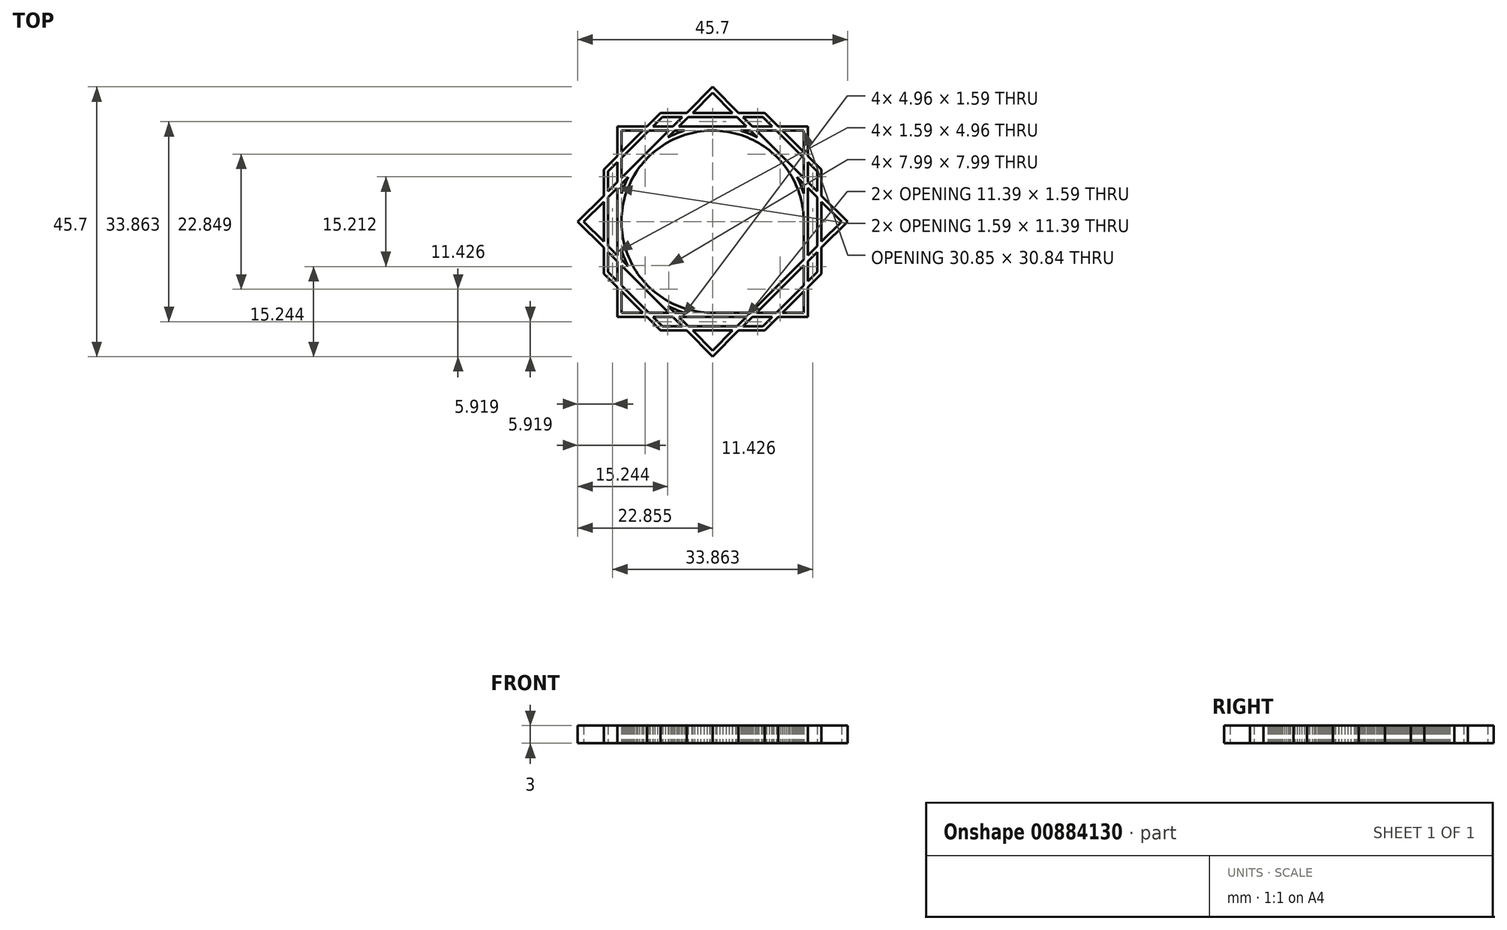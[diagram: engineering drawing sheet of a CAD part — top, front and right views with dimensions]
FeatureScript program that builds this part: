
annotation { "Feature Type Name" : "Feature", "Feature Type Description" : "" }
export const myFeature = defineFeature(function(context is Context, id is Id, definition is map)
    precondition{}
    {
        {
            var Q0;
            Q0=qCreatedBy(makeId("Top.planeOp"),FACE);
            var sketch = newSketch(context, id + "F0", { "sketchPlane" : qUnion([Q0])});
            skLineSegment(sketch, "E0", {"start": v(15.43, 0) * mm, "end": v(15.42, -0.54) * mm});
            skLineSegment(sketch, "E1", {"start": v(15.42, -0.54) * mm, "end": v(15.4, -1.07) * mm});
            skLineSegment(sketch, "E2", {"start": v(15.4, -1.07) * mm, "end": v(15.35, -1.6) * mm});
            skLineSegment(sketch, "E3", {"start": v(15.35, -1.6) * mm, "end": v(15.28, -2.14) * mm});
            skLineSegment(sketch, "E4", {"start": v(15.28, -2.14) * mm, "end": v(15.2, -2.66) * mm});
            skLineSegment(sketch, "E5", {"start": v(15.2, -2.66) * mm, "end": v(15.1, -3.2) * mm});
            skLineSegment(sketch, "E6", {"start": v(15.1, -3.2) * mm, "end": v(14.98, -3.71) * mm});
            skLineSegment(sketch, "E7", {"start": v(14.98, -3.71) * mm, "end": v(14.84, -4.23) * mm});
            skLineSegment(sketch, "E8", {"start": v(14.84, -4.23) * mm, "end": v(14.68, -4.74) * mm});
            skLineSegment(sketch, "E9", {"start": v(14.68, -4.74) * mm, "end": v(14.5, -5.25) * mm});
            skLineSegment(sketch, "E10", {"start": v(14.5, -5.25) * mm, "end": v(14.32, -5.75) * mm});
            skLineSegment(sketch, "E11", {"start": v(14.32, -5.75) * mm, "end": v(14.1, -6.24) * mm});
            skLineSegment(sketch, "E12", {"start": v(14.1, -6.24) * mm, "end": v(13.88, -6.73) * mm});
            skLineSegment(sketch, "E13", {"start": v(13.88, -6.73) * mm, "end": v(13.64, -7.2) * mm});
            skLineSegment(sketch, "E14", {"start": v(13.64, -7.2) * mm, "end": v(13.38, -7.68) * mm});
            skLineSegment(sketch, "E15", {"start": v(13.38, -7.68) * mm, "end": v(13.1, -8.14) * mm});
            skLineSegment(sketch, "E16", {"start": v(13.1, -8.14) * mm, "end": v(12.82, -8.59) * mm});
            skLineSegment(sketch, "E17", {"start": v(12.82, -8.59) * mm, "end": v(12.51, -9.03) * mm});
            skLineSegment(sketch, "E18", {"start": v(12.51, -9.03) * mm, "end": v(12.2, -9.45) * mm});
            skLineSegment(sketch, "E19", {"start": v(12.2, -9.45) * mm, "end": v(11.86, -9.87) * mm});
            skLineSegment(sketch, "E20", {"start": v(11.86, -9.87) * mm, "end": v(11.5, -10.28) * mm});
            skLineSegment(sketch, "E21", {"start": v(11.5, -10.28) * mm, "end": v(11.14, -10.67) * mm});
            skLineSegment(sketch, "E22", {"start": v(11.14, -10.67) * mm, "end": v(10.77, -11.05) * mm});
            skLineSegment(sketch, "E23", {"start": v(10.77, -11.05) * mm, "end": v(10.38, -11.42) * mm});
            skLineSegment(sketch, "E24", {"start": v(10.38, -11.42) * mm, "end": v(9.97, -11.77) * mm});
            skLineSegment(sketch, "E25", {"start": v(9.97, -11.77) * mm, "end": v(9.56, -12.11) * mm});
            skLineSegment(sketch, "E26", {"start": v(9.56, -12.11) * mm, "end": v(9.13, -12.44) * mm});
            skLineSegment(sketch, "E27", {"start": v(9.13, -12.44) * mm, "end": v(8.7, -12.74) * mm});
            skLineSegment(sketch, "E28", {"start": v(8.7, -12.74) * mm, "end": v(8.25, -13.04) * mm});
            skLineSegment(sketch, "E29", {"start": v(8.25, -13.04) * mm, "end": v(7.8, -13.32) * mm});
            skLineSegment(sketch, "E30", {"start": v(7.8, -13.32) * mm, "end": v(7.32, -13.58) * mm});
            skLineSegment(sketch, "E31", {"start": v(7.32, -13.58) * mm, "end": v(6.85, -13.83) * mm});
            skLineSegment(sketch, "E32", {"start": v(6.85, -13.83) * mm, "end": v(6.37, -14.06) * mm});
            skLineSegment(sketch, "E33", {"start": v(6.37, -14.06) * mm, "end": v(5.87, -14.27) * mm});
            skLineSegment(sketch, "E34", {"start": v(5.87, -14.27) * mm, "end": v(5.37, -14.46) * mm});
            skLineSegment(sketch, "E35", {"start": v(5.37, -14.46) * mm, "end": v(4.87, -14.64) * mm});
            skLineSegment(sketch, "E36", {"start": v(4.87, -14.64) * mm, "end": v(4.36, -14.8) * mm});
            skLineSegment(sketch, "E37", {"start": v(4.36, -14.8) * mm, "end": v(3.84, -14.94) * mm});
            skLineSegment(sketch, "E38", {"start": v(3.84, -14.94) * mm, "end": v(3.32, -15.07) * mm});
            skLineSegment(sketch, "E39", {"start": v(3.32, -15.07) * mm, "end": v(2.8, -15.17) * mm});
            skLineSegment(sketch, "E40", {"start": v(2.8, -15.17) * mm, "end": v(2.27, -15.26) * mm});
            skLineSegment(sketch, "E41", {"start": v(2.27, -15.26) * mm, "end": v(1.74, -15.33) * mm});
            skLineSegment(sketch, "E42", {"start": v(1.74, -15.33) * mm, "end": v(1.2, -15.38) * mm});
            skLineSegment(sketch, "E43", {"start": v(1.2, -15.38) * mm, "end": v(0.67, -15.41) * mm});
            skLineSegment(sketch, "E44", {"start": v(0.67, -15.41) * mm, "end": v(0.13, -15.43) * mm});
            skLineSegment(sketch, "E45", {"start": v(0.13, -15.43) * mm, "end": v(-0.4, -15.42) * mm});
            skLineSegment(sketch, "E46", {"start": v(-0.4, -15.42) * mm, "end": v(-0.94, -15.4) * mm});
            skLineSegment(sketch, "E47", {"start": v(-0.94, -15.4) * mm, "end": v(-1.47, -15.36) * mm});
            skLineSegment(sketch, "E48", {"start": v(-1.47, -15.36) * mm, "end": v(-2, -15.3) * mm});
            skLineSegment(sketch, "E49", {"start": v(-2, -15.3) * mm, "end": v(-2.53, -15.22) * mm});
            skLineSegment(sketch, "E50", {"start": v(-2.53, -15.22) * mm, "end": v(-3.06, -15.12) * mm});
            skLineSegment(sketch, "E51", {"start": v(-3.06, -15.12) * mm, "end": v(-3.58, -15) * mm});
            skLineSegment(sketch, "E52", {"start": v(-3.58, -15) * mm, "end": v(-4.1, -14.87) * mm});
            skLineSegment(sketch, "E53", {"start": v(-4.1, -14.87) * mm, "end": v(-4.61, -14.72) * mm});
            skLineSegment(sketch, "E54", {"start": v(-4.61, -14.72) * mm, "end": v(-5.12, -14.55) * mm});
            skLineSegment(sketch, "E55", {"start": v(-5.12, -14.55) * mm, "end": v(-5.63, -14.37) * mm});
            skLineSegment(sketch, "E56", {"start": v(-5.63, -14.37) * mm, "end": v(-6.12, -14.16) * mm});
            skLineSegment(sketch, "E57", {"start": v(-6.12, -14.16) * mm, "end": v(-6.6, -13.94) * mm});
            skLineSegment(sketch, "E58", {"start": v(-6.6, -13.94) * mm, "end": v(-7.09, -13.7) * mm});
            skLineSegment(sketch, "E59", {"start": v(-7.09, -13.7) * mm, "end": v(-7.56, -13.45) * mm});
            skLineSegment(sketch, "E60", {"start": v(-7.56, -13.45) * mm, "end": v(-8.02, -13.18) * mm});
            skLineSegment(sketch, "E61", {"start": v(-8.02, -13.18) * mm, "end": v(-8.47, -12.9) * mm});
            skLineSegment(sketch, "E62", {"start": v(-8.47, -12.9) * mm, "end": v(-8.92, -12.6) * mm});
            skLineSegment(sketch, "E63", {"start": v(-8.92, -12.6) * mm, "end": v(-9.35, -12.27) * mm});
            skLineSegment(sketch, "E64", {"start": v(-9.35, -12.27) * mm, "end": v(-9.77, -11.94) * mm});
            skLineSegment(sketch, "E65", {"start": v(-9.77, -11.94) * mm, "end": v(-10.18, -11.6) * mm});
            skLineSegment(sketch, "E66", {"start": v(-10.18, -11.6) * mm, "end": v(-10.57, -11.24) * mm});
            skLineSegment(sketch, "E67", {"start": v(-10.57, -11.24) * mm, "end": v(-10.96, -10.86) * mm});
            skLineSegment(sketch, "E68", {"start": v(-10.96, -10.86) * mm, "end": v(-11.33, -10.48) * mm});
            skLineSegment(sketch, "E69", {"start": v(-11.33, -10.48) * mm, "end": v(-11.68, -10.08) * mm});
            skLineSegment(sketch, "E70", {"start": v(-11.68, -10.08) * mm, "end": v(-12.03, -9.66) * mm});
            skLineSegment(sketch, "E71", {"start": v(-12.03, -9.66) * mm, "end": v(-12.36, -9.24) * mm});
            skLineSegment(sketch, "E72", {"start": v(-12.36, -9.24) * mm, "end": v(-12.67, -8.8) * mm});
            skLineSegment(sketch, "E73", {"start": v(-12.67, -8.8) * mm, "end": v(-12.97, -8.36) * mm});
            skLineSegment(sketch, "E74", {"start": v(-12.97, -8.36) * mm, "end": v(-13.25, -7.9) * mm});
            skLineSegment(sketch, "E75", {"start": v(-13.25, -7.9) * mm, "end": v(-13.52, -7.44) * mm});
            skLineSegment(sketch, "E76", {"start": v(-13.52, -7.44) * mm, "end": v(-13.77, -6.97) * mm});
            skLineSegment(sketch, "E77", {"start": v(-13.77, -6.97) * mm, "end": v(-14, -6.49) * mm});
            skLineSegment(sketch, "E78", {"start": v(-14, -6.49) * mm, "end": v(-14.22, -6) * mm});
            skLineSegment(sketch, "E79", {"start": v(-14.22, -6) * mm, "end": v(-14.42, -5.5) * mm});
            skLineSegment(sketch, "E80", {"start": v(-14.42, -5.5) * mm, "end": v(-14.6, -5) * mm});
            skLineSegment(sketch, "E81", {"start": v(-14.6, -5) * mm, "end": v(-14.76, -4.49) * mm});
            skLineSegment(sketch, "E82", {"start": v(-14.76, -4.49) * mm, "end": v(-14.9, -3.97) * mm});
            skLineSegment(sketch, "E83", {"start": v(-14.9, -3.97) * mm, "end": v(-15.04, -3.45) * mm});
            skLineSegment(sketch, "E84", {"start": v(-15.04, -3.45) * mm, "end": v(-15.15, -2.93) * mm});
            skLineSegment(sketch, "E85", {"start": v(-15.15, -2.93) * mm, "end": v(-15.24, -2.4) * mm});
            skLineSegment(sketch, "E86", {"start": v(-15.24, -2.4) * mm, "end": v(-15.32, -1.87) * mm});
            skLineSegment(sketch, "E87", {"start": v(-15.32, -1.87) * mm, "end": v(-15.37, -1.34) * mm});
            skLineSegment(sketch, "E88", {"start": v(-15.37, -1.34) * mm, "end": v(-15.4, -0.8) * mm});
            skLineSegment(sketch, "E89", {"start": v(-15.4, -0.8) * mm, "end": v(-15.43, -0.27) * mm});
            skLineSegment(sketch, "E90", {"start": v(-15.43, -0.27) * mm, "end": v(-15.43, 0.27) * mm});
            skLineSegment(sketch, "E91", {"start": v(-15.43, 0.27) * mm, "end": v(-15.4, 0.8) * mm});
            skLineSegment(sketch, "E92", {"start": v(-15.4, 0.8) * mm, "end": v(-15.37, 1.34) * mm});
            skLineSegment(sketch, "E93", {"start": v(-15.37, 1.34) * mm, "end": v(-15.32, 1.87) * mm});
            skLineSegment(sketch, "E94", {"start": v(-15.32, 1.87) * mm, "end": v(-15.24, 2.4) * mm});
            skLineSegment(sketch, "E95", {"start": v(-15.24, 2.4) * mm, "end": v(-15.15, 2.93) * mm});
            skLineSegment(sketch, "E96", {"start": v(-15.15, 2.93) * mm, "end": v(-15.04, 3.45) * mm});
            skLineSegment(sketch, "E97", {"start": v(-15.04, 3.45) * mm, "end": v(-14.9, 3.97) * mm});
            skLineSegment(sketch, "E98", {"start": v(-14.9, 3.97) * mm, "end": v(-14.76, 4.49) * mm});
            skLineSegment(sketch, "E99", {"start": v(-14.76, 4.49) * mm, "end": v(-14.6, 5) * mm});
            skLineSegment(sketch, "E100", {"start": v(-14.6, 5) * mm, "end": v(-14.42, 5.5) * mm});
            skLineSegment(sketch, "E101", {"start": v(-14.42, 5.5) * mm, "end": v(-14.22, 6) * mm});
            skLineSegment(sketch, "E102", {"start": v(-14.22, 6) * mm, "end": v(-14, 6.49) * mm});
            skLineSegment(sketch, "E103", {"start": v(-14, 6.49) * mm, "end": v(-13.77, 6.97) * mm});
            skLineSegment(sketch, "E104", {"start": v(-13.77, 6.97) * mm, "end": v(-13.52, 7.44) * mm});
            skLineSegment(sketch, "E105", {"start": v(-13.52, 7.44) * mm, "end": v(-13.25, 7.9) * mm});
            skLineSegment(sketch, "E106", {"start": v(-13.25, 7.9) * mm, "end": v(-12.97, 8.36) * mm});
            skLineSegment(sketch, "E107", {"start": v(-12.97, 8.36) * mm, "end": v(-12.67, 8.8) * mm});
            skLineSegment(sketch, "E108", {"start": v(-12.67, 8.8) * mm, "end": v(-12.36, 9.24) * mm});
            skLineSegment(sketch, "E109", {"start": v(-12.36, 9.24) * mm, "end": v(-12.03, 9.66) * mm});
            skLineSegment(sketch, "E110", {"start": v(-12.03, 9.66) * mm, "end": v(-11.68, 10.08) * mm});
            skLineSegment(sketch, "E111", {"start": v(-11.68, 10.08) * mm, "end": v(-11.33, 10.48) * mm});
            skLineSegment(sketch, "E112", {"start": v(-11.33, 10.48) * mm, "end": v(-10.96, 10.86) * mm});
            skLineSegment(sketch, "E113", {"start": v(-10.96, 10.86) * mm, "end": v(-10.57, 11.24) * mm});
            skLineSegment(sketch, "E114", {"start": v(-10.57, 11.24) * mm, "end": v(-10.18, 11.6) * mm});
            skLineSegment(sketch, "E115", {"start": v(-10.18, 11.6) * mm, "end": v(-9.77, 11.94) * mm});
            skLineSegment(sketch, "E116", {"start": v(-9.77, 11.94) * mm, "end": v(-9.35, 12.27) * mm});
            skLineSegment(sketch, "E117", {"start": v(-9.35, 12.27) * mm, "end": v(-8.92, 12.6) * mm});
            skLineSegment(sketch, "E118", {"start": v(-8.92, 12.6) * mm, "end": v(-8.47, 12.9) * mm});
            skLineSegment(sketch, "E119", {"start": v(-8.47, 12.9) * mm, "end": v(-8.02, 13.18) * mm});
            skLineSegment(sketch, "E120", {"start": v(-8.02, 13.18) * mm, "end": v(-7.56, 13.45) * mm});
            skLineSegment(sketch, "E121", {"start": v(-7.56, 13.45) * mm, "end": v(-7.09, 13.7) * mm});
            skLineSegment(sketch, "E122", {"start": v(-7.09, 13.7) * mm, "end": v(-6.6, 13.94) * mm});
            skLineSegment(sketch, "E123", {"start": v(-6.6, 13.94) * mm, "end": v(-6.12, 14.16) * mm});
            skLineSegment(sketch, "E124", {"start": v(-6.12, 14.16) * mm, "end": v(-5.63, 14.37) * mm});
            skLineSegment(sketch, "E125", {"start": v(-5.63, 14.37) * mm, "end": v(-5.12, 14.55) * mm});
            skLineSegment(sketch, "E126", {"start": v(-5.12, 14.55) * mm, "end": v(-4.61, 14.72) * mm});
            skLineSegment(sketch, "E127", {"start": v(-4.61, 14.72) * mm, "end": v(-4.1, 14.87) * mm});
            skLineSegment(sketch, "E128", {"start": v(-4.1, 14.87) * mm, "end": v(-3.58, 15) * mm});
            skLineSegment(sketch, "E129", {"start": v(-3.58, 15) * mm, "end": v(-3.06, 15.12) * mm});
            skLineSegment(sketch, "E130", {"start": v(-3.06, 15.12) * mm, "end": v(-2.53, 15.22) * mm});
            skLineSegment(sketch, "E131", {"start": v(-2.53, 15.22) * mm, "end": v(-2, 15.3) * mm});
            skLineSegment(sketch, "E132", {"start": v(-2, 15.3) * mm, "end": v(-1.47, 15.36) * mm});
            skLineSegment(sketch, "E133", {"start": v(-1.47, 15.36) * mm, "end": v(-0.94, 15.4) * mm});
            skLineSegment(sketch, "E134", {"start": v(-0.94, 15.4) * mm, "end": v(-0.4, 15.42) * mm});
            skLineSegment(sketch, "E135", {"start": v(-0.4, 15.42) * mm, "end": v(0.13, 15.43) * mm});
            skLineSegment(sketch, "E136", {"start": v(0.13, 15.43) * mm, "end": v(0.67, 15.41) * mm});
            skLineSegment(sketch, "E137", {"start": v(0.67, 15.41) * mm, "end": v(1.2, 15.38) * mm});
            skLineSegment(sketch, "E138", {"start": v(1.2, 15.38) * mm, "end": v(1.74, 15.33) * mm});
            skLineSegment(sketch, "E139", {"start": v(1.74, 15.33) * mm, "end": v(2.27, 15.26) * mm});
            skLineSegment(sketch, "E140", {"start": v(2.27, 15.26) * mm, "end": v(2.8, 15.17) * mm});
            skLineSegment(sketch, "E141", {"start": v(2.8, 15.17) * mm, "end": v(3.32, 15.07) * mm});
            skLineSegment(sketch, "E142", {"start": v(3.32, 15.07) * mm, "end": v(3.84, 14.94) * mm});
            skLineSegment(sketch, "E143", {"start": v(3.84, 14.94) * mm, "end": v(4.36, 14.8) * mm});
            skLineSegment(sketch, "E144", {"start": v(4.36, 14.8) * mm, "end": v(4.87, 14.64) * mm});
            skLineSegment(sketch, "E145", {"start": v(4.87, 14.64) * mm, "end": v(5.37, 14.46) * mm});
            skLineSegment(sketch, "E146", {"start": v(5.37, 14.46) * mm, "end": v(5.87, 14.27) * mm});
            skLineSegment(sketch, "E147", {"start": v(5.87, 14.27) * mm, "end": v(6.37, 14.06) * mm});
            skLineSegment(sketch, "E148", {"start": v(6.37, 14.06) * mm, "end": v(6.85, 13.83) * mm});
            skLineSegment(sketch, "E149", {"start": v(6.85, 13.83) * mm, "end": v(7.32, 13.58) * mm});
            skLineSegment(sketch, "E150", {"start": v(7.32, 13.58) * mm, "end": v(7.8, 13.32) * mm});
            skLineSegment(sketch, "E151", {"start": v(7.8, 13.32) * mm, "end": v(8.25, 13.04) * mm});
            skLineSegment(sketch, "E152", {"start": v(8.25, 13.04) * mm, "end": v(8.7, 12.74) * mm});
            skLineSegment(sketch, "E153", {"start": v(8.7, 12.74) * mm, "end": v(9.13, 12.44) * mm});
            skLineSegment(sketch, "E154", {"start": v(9.13, 12.44) * mm, "end": v(9.56, 12.11) * mm});
            skLineSegment(sketch, "E155", {"start": v(9.56, 12.11) * mm, "end": v(9.97, 11.77) * mm});
            skLineSegment(sketch, "E156", {"start": v(9.97, 11.77) * mm, "end": v(10.38, 11.42) * mm});
            skLineSegment(sketch, "E157", {"start": v(10.38, 11.42) * mm, "end": v(10.77, 11.05) * mm});
            skLineSegment(sketch, "E158", {"start": v(10.77, 11.05) * mm, "end": v(11.14, 10.67) * mm});
            skLineSegment(sketch, "E159", {"start": v(11.14, 10.67) * mm, "end": v(11.5, 10.28) * mm});
            skLineSegment(sketch, "E160", {"start": v(11.5, 10.28) * mm, "end": v(11.86, 9.87) * mm});
            skLineSegment(sketch, "E161", {"start": v(11.86, 9.87) * mm, "end": v(12.2, 9.45) * mm});
            skLineSegment(sketch, "E162", {"start": v(12.2, 9.45) * mm, "end": v(12.51, 9.03) * mm});
            skLineSegment(sketch, "E163", {"start": v(12.51, 9.03) * mm, "end": v(12.82, 8.59) * mm});
            skLineSegment(sketch, "E164", {"start": v(12.82, 8.59) * mm, "end": v(13.1, 8.14) * mm});
            skLineSegment(sketch, "E165", {"start": v(13.1, 8.14) * mm, "end": v(13.38, 7.68) * mm});
            skLineSegment(sketch, "E166", {"start": v(13.38, 7.68) * mm, "end": v(13.64, 7.2) * mm});
            skLineSegment(sketch, "E167", {"start": v(13.64, 7.2) * mm, "end": v(13.88, 6.73) * mm});
            skLineSegment(sketch, "E168", {"start": v(13.88, 6.73) * mm, "end": v(14.1, 6.24) * mm});
            skLineSegment(sketch, "E169", {"start": v(14.1, 6.24) * mm, "end": v(14.32, 5.75) * mm});
            skLineSegment(sketch, "E170", {"start": v(14.32, 5.75) * mm, "end": v(14.5, 5.25) * mm});
            skLineSegment(sketch, "E171", {"start": v(14.5, 5.25) * mm, "end": v(14.68, 4.74) * mm});
            skLineSegment(sketch, "E172", {"start": v(14.68, 4.74) * mm, "end": v(14.84, 4.23) * mm});
            skLineSegment(sketch, "E173", {"start": v(14.84, 4.23) * mm, "end": v(14.98, 3.71) * mm});
            skLineSegment(sketch, "E174", {"start": v(14.98, 3.71) * mm, "end": v(15.1, 3.2) * mm});
            skLineSegment(sketch, "E175", {"start": v(15.1, 3.2) * mm, "end": v(15.2, 2.66) * mm});
            skLineSegment(sketch, "E176", {"start": v(15.2, 2.66) * mm, "end": v(15.28, 2.14) * mm});
            skLineSegment(sketch, "E177", {"start": v(15.28, 2.14) * mm, "end": v(15.35, 1.6) * mm});
            skLineSegment(sketch, "E178", {"start": v(15.35, 1.6) * mm, "end": v(15.4, 1.07) * mm});
            skLineSegment(sketch, "E179", {"start": v(15.4, 1.07) * mm, "end": v(15.42, 0.54) * mm});
            skLineSegment(sketch, "E180", {"start": v(15.42, 0.54) * mm, "end": v(15.43, 0) * mm});
            skLineSegment(sketch, "E181", {"start": v(16.15, 0) * mm, "end": v(16.14, -0.56) * mm});
            skLineSegment(sketch, "E182", {"start": v(16.14, -0.56) * mm, "end": v(16.1, -1.12) * mm});
            skLineSegment(sketch, "E183", {"start": v(16.1, -1.12) * mm, "end": v(16.06, -1.68) * mm});
            skLineSegment(sketch, "E184", {"start": v(16.06, -1.68) * mm, "end": v(16, -2.24) * mm});
            skLineSegment(sketch, "E185", {"start": v(16, -2.24) * mm, "end": v(15.9, -2.79) * mm});
            skLineSegment(sketch, "E186", {"start": v(15.9, -2.79) * mm, "end": v(15.8, -3.34) * mm});
            skLineSegment(sketch, "E187", {"start": v(15.8, -3.34) * mm, "end": v(15.67, -3.89) * mm});
            skLineSegment(sketch, "E188", {"start": v(15.67, -3.89) * mm, "end": v(15.53, -4.43) * mm});
            skLineSegment(sketch, "E189", {"start": v(15.53, -4.43) * mm, "end": v(15.37, -4.96) * mm});
            skLineSegment(sketch, "E190", {"start": v(15.37, -4.96) * mm, "end": v(15.18, -5.5) * mm});
            skLineSegment(sketch, "E191", {"start": v(15.18, -5.5) * mm, "end": v(14.99, -6.02) * mm});
            skLineSegment(sketch, "E192", {"start": v(14.99, -6.02) * mm, "end": v(14.77, -6.53) * mm});
            skLineSegment(sketch, "E193", {"start": v(14.77, -6.53) * mm, "end": v(14.53, -7.04) * mm});
            skLineSegment(sketch, "E194", {"start": v(14.53, -7.04) * mm, "end": v(14.28, -7.54) * mm});
            skLineSegment(sketch, "E195", {"start": v(14.28, -7.54) * mm, "end": v(14, -8.03) * mm});
            skLineSegment(sketch, "E196", {"start": v(14, -8.03) * mm, "end": v(13.72, -8.51) * mm});
            skLineSegment(sketch, "E197", {"start": v(13.72, -8.51) * mm, "end": v(13.42, -8.99) * mm});
            skLineSegment(sketch, "E198", {"start": v(13.42, -8.99) * mm, "end": v(13.1, -9.45) * mm});
            skLineSegment(sketch, "E199", {"start": v(13.1, -9.45) * mm, "end": v(12.76, -9.9) * mm});
            skLineSegment(sketch, "E200", {"start": v(12.76, -9.9) * mm, "end": v(12.41, -10.33) * mm});
            skLineSegment(sketch, "E201", {"start": v(12.41, -10.33) * mm, "end": v(12.04, -10.76) * mm});
            skLineSegment(sketch, "E202", {"start": v(12.04, -10.76) * mm, "end": v(11.66, -11.17) * mm});
            skLineSegment(sketch, "E203", {"start": v(11.66, -11.17) * mm, "end": v(11.27, -11.57) * mm});
            skLineSegment(sketch, "E204", {"start": v(11.27, -11.57) * mm, "end": v(10.86, -11.95) * mm});
            skLineSegment(sketch, "E205", {"start": v(10.86, -11.95) * mm, "end": v(10.44, -12.32) * mm});
            skLineSegment(sketch, "E206", {"start": v(10.44, -12.32) * mm, "end": v(10, -12.67) * mm});
            skLineSegment(sketch, "E207", {"start": v(10, -12.67) * mm, "end": v(9.56, -13.01) * mm});
            skLineSegment(sketch, "E208", {"start": v(9.56, -13.01) * mm, "end": v(9.1, -13.34) * mm});
            skLineSegment(sketch, "E209", {"start": v(9.1, -13.34) * mm, "end": v(8.63, -13.65) * mm});
            skLineSegment(sketch, "E210", {"start": v(8.63, -13.65) * mm, "end": v(8.15, -13.94) * mm});
            skLineSegment(sketch, "E211", {"start": v(8.15, -13.94) * mm, "end": v(7.67, -14.21) * mm});
            skLineSegment(sketch, "E212", {"start": v(7.67, -14.21) * mm, "end": v(7.17, -14.47) * mm});
            skLineSegment(sketch, "E213", {"start": v(7.17, -14.47) * mm, "end": v(6.66, -14.7) * mm});
            skLineSegment(sketch, "E214", {"start": v(6.66, -14.7) * mm, "end": v(6.15, -14.93) * mm});
            skLineSegment(sketch, "E215", {"start": v(6.15, -14.93) * mm, "end": v(5.63, -15.14) * mm});
            skLineSegment(sketch, "E216", {"start": v(5.63, -15.14) * mm, "end": v(5.1, -15.32) * mm});
            skLineSegment(sketch, "E217", {"start": v(5.1, -15.32) * mm, "end": v(4.56, -15.5) * mm});
            skLineSegment(sketch, "E218", {"start": v(4.56, -15.5) * mm, "end": v(4.02, -15.64) * mm});
            skLineSegment(sketch, "E219", {"start": v(4.02, -15.64) * mm, "end": v(3.48, -15.77) * mm});
            skLineSegment(sketch, "E220", {"start": v(3.48, -15.77) * mm, "end": v(2.93, -15.88) * mm});
            skLineSegment(sketch, "E221", {"start": v(2.93, -15.88) * mm, "end": v(2.37, -15.97) * mm});
            skLineSegment(sketch, "E222", {"start": v(2.37, -15.97) * mm, "end": v(1.82, -16.05) * mm});
            skLineSegment(sketch, "E223", {"start": v(1.82, -16.05) * mm, "end": v(1.26, -16.1) * mm});
            skLineSegment(sketch, "E224", {"start": v(1.26, -16.1) * mm, "end": v(0.7, -16.13) * mm});
            skLineSegment(sketch, "E225", {"start": v(0.7, -16.13) * mm, "end": v(0.14, -16.15) * mm});
            skLineSegment(sketch, "E226", {"start": v(0.14, -16.15) * mm, "end": v(-0.42, -16.14) * mm});
            skLineSegment(sketch, "E227", {"start": v(-0.42, -16.14) * mm, "end": v(-0.98, -16.12) * mm});
            skLineSegment(sketch, "E228", {"start": v(-0.98, -16.12) * mm, "end": v(-1.54, -16.07) * mm});
            skLineSegment(sketch, "E229", {"start": v(-1.54, -16.07) * mm, "end": v(-2.1, -16.01) * mm});
            skLineSegment(sketch, "E230", {"start": v(-2.1, -16.01) * mm, "end": v(-2.65, -15.93) * mm});
            skLineSegment(sketch, "E231", {"start": v(-2.65, -15.93) * mm, "end": v(-3.2, -15.83) * mm});
            skLineSegment(sketch, "E232", {"start": v(-3.2, -15.83) * mm, "end": v(-3.75, -15.7) * mm});
            skLineSegment(sketch, "E233", {"start": v(-3.75, -15.7) * mm, "end": v(-4.3, -15.57) * mm});
            skLineSegment(sketch, "E234", {"start": v(-4.3, -15.57) * mm, "end": v(-4.83, -15.4) * mm});
            skLineSegment(sketch, "E235", {"start": v(-4.83, -15.4) * mm, "end": v(-5.36, -15.23) * mm});
            skLineSegment(sketch, "E236", {"start": v(-5.36, -15.23) * mm, "end": v(-5.89, -15.04) * mm});
            skLineSegment(sketch, "E237", {"start": v(-5.89, -15.04) * mm, "end": v(-6.4, -14.82) * mm});
            skLineSegment(sketch, "E238", {"start": v(-6.4, -14.82) * mm, "end": v(-6.92, -14.6) * mm});
            skLineSegment(sketch, "E239", {"start": v(-6.92, -14.6) * mm, "end": v(-7.42, -14.34) * mm});
            skLineSegment(sketch, "E240", {"start": v(-7.42, -14.34) * mm, "end": v(-7.91, -14.08) * mm});
            skLineSegment(sketch, "E241", {"start": v(-7.91, -14.08) * mm, "end": v(-8.4, -13.8) * mm});
            skLineSegment(sketch, "E242", {"start": v(-8.4, -13.8) * mm, "end": v(-8.87, -13.5) * mm});
            skLineSegment(sketch, "E243", {"start": v(-8.87, -13.5) * mm, "end": v(-9.33, -13.18) * mm});
            skLineSegment(sketch, "E244", {"start": v(-9.33, -13.18) * mm, "end": v(-9.78, -12.85) * mm});
            skLineSegment(sketch, "E245", {"start": v(-9.78, -12.85) * mm, "end": v(-10.22, -12.5) * mm});
            skLineSegment(sketch, "E246", {"start": v(-10.22, -12.5) * mm, "end": v(-10.65, -12.14) * mm});
            skLineSegment(sketch, "E247", {"start": v(-10.65, -12.14) * mm, "end": v(-11.07, -11.76) * mm});
            skLineSegment(sketch, "E248", {"start": v(-11.07, -11.76) * mm, "end": v(-11.47, -11.37) * mm});
            skLineSegment(sketch, "E249", {"start": v(-11.47, -11.37) * mm, "end": v(-11.86, -10.96) * mm});
            skLineSegment(sketch, "E250", {"start": v(-11.86, -10.96) * mm, "end": v(-12.23, -10.55) * mm});
            skLineSegment(sketch, "E251", {"start": v(-12.23, -10.55) * mm, "end": v(-12.59, -10.12) * mm});
            skLineSegment(sketch, "E252", {"start": v(-12.59, -10.12) * mm, "end": v(-12.93, -9.67) * mm});
            skLineSegment(sketch, "E253", {"start": v(-12.93, -9.67) * mm, "end": v(-13.26, -9.22) * mm});
            skLineSegment(sketch, "E254", {"start": v(-13.26, -9.22) * mm, "end": v(-13.57, -8.75) * mm});
            skLineSegment(sketch, "E255", {"start": v(-13.57, -8.75) * mm, "end": v(-13.87, -8.28) * mm});
            skLineSegment(sketch, "E256", {"start": v(-13.87, -8.28) * mm, "end": v(-14.15, -7.79) * mm});
            skLineSegment(sketch, "E257", {"start": v(-14.15, -7.79) * mm, "end": v(-14.4, -7.3) * mm});
            skLineSegment(sketch, "E258", {"start": v(-14.4, -7.3) * mm, "end": v(-14.65, -6.79) * mm});
            skLineSegment(sketch, "E259", {"start": v(-14.65, -6.79) * mm, "end": v(-14.88, -6.28) * mm});
            skLineSegment(sketch, "E260", {"start": v(-14.88, -6.28) * mm, "end": v(-15.09, -5.76) * mm});
            skLineSegment(sketch, "E261", {"start": v(-15.09, -5.76) * mm, "end": v(-15.28, -5.23) * mm});
            skLineSegment(sketch, "E262", {"start": v(-15.28, -5.23) * mm, "end": v(-15.45, -4.7) * mm});
            skLineSegment(sketch, "E263", {"start": v(-15.45, -4.7) * mm, "end": v(-15.6, -4.16) * mm});
            skLineSegment(sketch, "E264", {"start": v(-15.6, -4.16) * mm, "end": v(-15.74, -3.61) * mm});
            skLineSegment(sketch, "E265", {"start": v(-15.74, -3.61) * mm, "end": v(-15.85, -3.06) * mm});
            skLineSegment(sketch, "E266", {"start": v(-15.85, -3.06) * mm, "end": v(-15.95, -2.51) * mm});
            skLineSegment(sketch, "E267", {"start": v(-15.95, -2.51) * mm, "end": v(-16.03, -1.96) * mm});
            skLineSegment(sketch, "E268", {"start": v(-16.03, -1.96) * mm, "end": v(-16.09, -1.4) * mm});
            skLineSegment(sketch, "E269", {"start": v(-16.09, -1.4) * mm, "end": v(-16.13, -0.84) * mm});
            skLineSegment(sketch, "E270", {"start": v(-16.13, -0.84) * mm, "end": v(-16.15, -0.28) * mm});
            skLineSegment(sketch, "E271", {"start": v(-16.15, -0.28) * mm, "end": v(-16.15, 0.28) * mm});
            skLineSegment(sketch, "E272", {"start": v(-16.15, 0.28) * mm, "end": v(-16.13, 0.84) * mm});
            skLineSegment(sketch, "E273", {"start": v(-16.13, 0.84) * mm, "end": v(-16.09, 1.4) * mm});
            skLineSegment(sketch, "E274", {"start": v(-16.09, 1.4) * mm, "end": v(-16.03, 1.96) * mm});
            skLineSegment(sketch, "E275", {"start": v(-16.03, 1.96) * mm, "end": v(-15.95, 2.51) * mm});
            skLineSegment(sketch, "E276", {"start": v(-15.95, 2.51) * mm, "end": v(-15.85, 3.06) * mm});
            skLineSegment(sketch, "E277", {"start": v(-15.85, 3.06) * mm, "end": v(-15.74, 3.61) * mm});
            skLineSegment(sketch, "E278", {"start": v(-15.74, 3.61) * mm, "end": v(-15.6, 4.16) * mm});
            skLineSegment(sketch, "E279", {"start": v(-15.6, 4.16) * mm, "end": v(-15.45, 4.7) * mm});
            skLineSegment(sketch, "E280", {"start": v(-15.45, 4.7) * mm, "end": v(-15.28, 5.23) * mm});
            skLineSegment(sketch, "E281", {"start": v(-15.28, 5.23) * mm, "end": v(-15.09, 5.76) * mm});
            skLineSegment(sketch, "E282", {"start": v(-15.09, 5.76) * mm, "end": v(-14.88, 6.28) * mm});
            skLineSegment(sketch, "E283", {"start": v(-14.88, 6.28) * mm, "end": v(-14.65, 6.79) * mm});
            skLineSegment(sketch, "E284", {"start": v(-14.65, 6.79) * mm, "end": v(-14.4, 7.3) * mm});
            skLineSegment(sketch, "E285", {"start": v(-14.4, 7.3) * mm, "end": v(-14.15, 7.79) * mm});
            skLineSegment(sketch, "E286", {"start": v(-14.15, 7.79) * mm, "end": v(-13.87, 8.28) * mm});
            skLineSegment(sketch, "E287", {"start": v(-13.87, 8.28) * mm, "end": v(-13.57, 8.75) * mm});
            skLineSegment(sketch, "E288", {"start": v(-13.57, 8.75) * mm, "end": v(-13.26, 9.22) * mm});
            skLineSegment(sketch, "E289", {"start": v(-13.26, 9.22) * mm, "end": v(-12.93, 9.67) * mm});
            skLineSegment(sketch, "E290", {"start": v(-12.93, 9.67) * mm, "end": v(-12.59, 10.12) * mm});
            skLineSegment(sketch, "E291", {"start": v(-12.59, 10.12) * mm, "end": v(-12.23, 10.55) * mm});
            skLineSegment(sketch, "E292", {"start": v(-12.23, 10.55) * mm, "end": v(-11.86, 10.96) * mm});
            skLineSegment(sketch, "E293", {"start": v(-11.86, 10.96) * mm, "end": v(-11.47, 11.37) * mm});
            skLineSegment(sketch, "E294", {"start": v(-11.47, 11.37) * mm, "end": v(-11.07, 11.76) * mm});
            skLineSegment(sketch, "E295", {"start": v(-11.07, 11.76) * mm, "end": v(-10.65, 12.14) * mm});
            skLineSegment(sketch, "E296", {"start": v(-10.65, 12.14) * mm, "end": v(-10.22, 12.5) * mm});
            skLineSegment(sketch, "E297", {"start": v(-10.22, 12.5) * mm, "end": v(-9.78, 12.85) * mm});
            skLineSegment(sketch, "E298", {"start": v(-9.78, 12.85) * mm, "end": v(-9.33, 13.18) * mm});
            skLineSegment(sketch, "E299", {"start": v(-9.33, 13.18) * mm, "end": v(-8.87, 13.5) * mm});
            skLineSegment(sketch, "E300", {"start": v(-8.87, 13.5) * mm, "end": v(-8.4, 13.8) * mm});
            skLineSegment(sketch, "E301", {"start": v(-8.4, 13.8) * mm, "end": v(-7.91, 14.08) * mm});
            skLineSegment(sketch, "E302", {"start": v(-7.91, 14.08) * mm, "end": v(-7.42, 14.34) * mm});
            skLineSegment(sketch, "E303", {"start": v(-7.42, 14.34) * mm, "end": v(-6.92, 14.6) * mm});
            skLineSegment(sketch, "E304", {"start": v(-6.92, 14.6) * mm, "end": v(-6.4, 14.82) * mm});
            skLineSegment(sketch, "E305", {"start": v(-6.4, 14.82) * mm, "end": v(-5.89, 15.04) * mm});
            skLineSegment(sketch, "E306", {"start": v(-5.89, 15.04) * mm, "end": v(-5.36, 15.23) * mm});
            skLineSegment(sketch, "E307", {"start": v(-5.36, 15.23) * mm, "end": v(-4.83, 15.4) * mm});
            skLineSegment(sketch, "E308", {"start": v(-4.83, 15.4) * mm, "end": v(-4.3, 15.57) * mm});
            skLineSegment(sketch, "E309", {"start": v(-4.3, 15.57) * mm, "end": v(-3.75, 15.7) * mm});
            skLineSegment(sketch, "E310", {"start": v(-3.75, 15.7) * mm, "end": v(-3.2, 15.83) * mm});
            skLineSegment(sketch, "E311", {"start": v(-3.2, 15.83) * mm, "end": v(-2.65, 15.93) * mm});
            skLineSegment(sketch, "E312", {"start": v(-2.65, 15.93) * mm, "end": v(-2.1, 16.01) * mm});
            skLineSegment(sketch, "E313", {"start": v(-2.1, 16.01) * mm, "end": v(-1.54, 16.07) * mm});
            skLineSegment(sketch, "E314", {"start": v(-1.54, 16.07) * mm, "end": v(-0.98, 16.12) * mm});
            skLineSegment(sketch, "E315", {"start": v(-0.98, 16.12) * mm, "end": v(-0.42, 16.14) * mm});
            skLineSegment(sketch, "E316", {"start": v(-0.42, 16.14) * mm, "end": v(0.14, 16.15) * mm});
            skLineSegment(sketch, "E317", {"start": v(0.14, 16.15) * mm, "end": v(0.7, 16.13) * mm});
            skLineSegment(sketch, "E318", {"start": v(0.7, 16.13) * mm, "end": v(1.26, 16.1) * mm});
            skLineSegment(sketch, "E319", {"start": v(1.26, 16.1) * mm, "end": v(1.82, 16.05) * mm});
            skLineSegment(sketch, "E320", {"start": v(1.82, 16.05) * mm, "end": v(2.37, 15.97) * mm});
            skLineSegment(sketch, "E321", {"start": v(2.37, 15.97) * mm, "end": v(2.93, 15.88) * mm});
            skLineSegment(sketch, "E322", {"start": v(2.93, 15.88) * mm, "end": v(3.48, 15.77) * mm});
            skLineSegment(sketch, "E323", {"start": v(3.48, 15.77) * mm, "end": v(4.02, 15.64) * mm});
            skLineSegment(sketch, "E324", {"start": v(4.02, 15.64) * mm, "end": v(4.56, 15.5) * mm});
            skLineSegment(sketch, "E325", {"start": v(4.56, 15.5) * mm, "end": v(5.1, 15.32) * mm});
            skLineSegment(sketch, "E326", {"start": v(5.1, 15.32) * mm, "end": v(5.63, 15.14) * mm});
            skLineSegment(sketch, "E327", {"start": v(5.63, 15.14) * mm, "end": v(6.15, 14.93) * mm});
            skLineSegment(sketch, "E328", {"start": v(6.15, 14.93) * mm, "end": v(6.66, 14.7) * mm});
            skLineSegment(sketch, "E329", {"start": v(6.66, 14.7) * mm, "end": v(7.17, 14.47) * mm});
            skLineSegment(sketch, "E330", {"start": v(7.17, 14.47) * mm, "end": v(7.67, 14.21) * mm});
            skLineSegment(sketch, "E331", {"start": v(7.67, 14.21) * mm, "end": v(8.15, 13.94) * mm});
            skLineSegment(sketch, "E332", {"start": v(8.15, 13.94) * mm, "end": v(8.63, 13.65) * mm});
            skLineSegment(sketch, "E333", {"start": v(8.63, 13.65) * mm, "end": v(9.1, 13.34) * mm});
            skLineSegment(sketch, "E334", {"start": v(9.1, 13.34) * mm, "end": v(9.56, 13.01) * mm});
            skLineSegment(sketch, "E335", {"start": v(9.56, 13.01) * mm, "end": v(10, 12.67) * mm});
            skLineSegment(sketch, "E336", {"start": v(10, 12.67) * mm, "end": v(10.44, 12.32) * mm});
            skLineSegment(sketch, "E337", {"start": v(10.44, 12.32) * mm, "end": v(10.86, 11.95) * mm});
            skLineSegment(sketch, "E338", {"start": v(10.86, 11.95) * mm, "end": v(11.27, 11.57) * mm});
            skLineSegment(sketch, "E339", {"start": v(11.27, 11.57) * mm, "end": v(11.66, 11.17) * mm});
            skLineSegment(sketch, "E340", {"start": v(11.66, 11.17) * mm, "end": v(12.04, 10.76) * mm});
            skLineSegment(sketch, "E341", {"start": v(12.04, 10.76) * mm, "end": v(12.41, 10.33) * mm});
            skLineSegment(sketch, "E342", {"start": v(12.41, 10.33) * mm, "end": v(12.76, 9.9) * mm});
            skLineSegment(sketch, "E343", {"start": v(12.76, 9.9) * mm, "end": v(13.1, 9.45) * mm});
            skLineSegment(sketch, "E344", {"start": v(13.1, 9.45) * mm, "end": v(13.42, 8.99) * mm});
            skLineSegment(sketch, "E345", {"start": v(13.42, 8.99) * mm, "end": v(13.72, 8.51) * mm});
            skLineSegment(sketch, "E346", {"start": v(13.72, 8.51) * mm, "end": v(14, 8.03) * mm});
            skLineSegment(sketch, "E347", {"start": v(14, 8.03) * mm, "end": v(14.28, 7.54) * mm});
            skLineSegment(sketch, "E348", {"start": v(14.28, 7.54) * mm, "end": v(14.53, 7.04) * mm});
            skLineSegment(sketch, "E349", {"start": v(14.53, 7.04) * mm, "end": v(14.77, 6.53) * mm});
            skLineSegment(sketch, "E350", {"start": v(14.77, 6.53) * mm, "end": v(14.99, 6.02) * mm});
            skLineSegment(sketch, "E351", {"start": v(14.99, 6.02) * mm, "end": v(15.18, 5.5) * mm});
            skLineSegment(sketch, "E352", {"start": v(15.18, 5.5) * mm, "end": v(15.37, 4.96) * mm});
            skLineSegment(sketch, "E353", {"start": v(15.37, 4.96) * mm, "end": v(15.53, 4.43) * mm});
            skLineSegment(sketch, "E354", {"start": v(15.53, 4.43) * mm, "end": v(15.67, 3.89) * mm});
            skLineSegment(sketch, "E355", {"start": v(15.67, 3.89) * mm, "end": v(15.8, 3.34) * mm});
            skLineSegment(sketch, "E356", {"start": v(15.8, 3.34) * mm, "end": v(15.9, 2.79) * mm});
            skLineSegment(sketch, "E357", {"start": v(15.9, 2.79) * mm, "end": v(16, 2.24) * mm});
            skLineSegment(sketch, "E358", {"start": v(16, 2.24) * mm, "end": v(16.06, 1.68) * mm});
            skLineSegment(sketch, "E359", {"start": v(16.06, 1.68) * mm, "end": v(16.1, 1.12) * mm});
            skLineSegment(sketch, "E360", {"start": v(16.1, 1.12) * mm, "end": v(16.14, 0.56) * mm});
            skLineSegment(sketch, "E361", {"start": v(16.14, 0.56) * mm, "end": v(16.15, 0) * mm});
            skLineSegment(sketch, "E362", {"start": v(15.42, -15.42) * mm, "end": v(-15.42, -15.42) * mm});
            skLineSegment(sketch, "E363", {"start": v(-15.42, -15.42) * mm, "end": v(-15.42, 15.42) * mm});
            skLineSegment(sketch, "E364", {"start": v(-15.42, 15.42) * mm, "end": v(15.42, 15.42) * mm});
            skLineSegment(sketch, "E365", {"start": v(15.42, 15.42) * mm, "end": v(15.42, -15.42) * mm});
            skLineSegment(sketch, "E366", {"start": v(16.14, -16.14) * mm, "end": v(-16.14, -16.14) * mm});
            skLineSegment(sketch, "E367", {"start": v(-16.14, -16.14) * mm, "end": v(-16.14, 16.14) * mm});
            skLineSegment(sketch, "E368", {"start": v(-16.14, 16.14) * mm, "end": v(16.14, 16.14) * mm});
            skLineSegment(sketch, "E369", {"start": v(16.14, 16.14) * mm, "end": v(16.14, -16.14) * mm});
            skLineSegment(sketch, "E370", {"start": v(18.44, 8.8) * mm, "end": v(8.8, 18.44) * mm});
            skLineSegment(sketch, "E371", {"start": v(8.8, 18.44) * mm, "end": v(-8.8, 18.44) * mm});
            skLineSegment(sketch, "E372", {"start": v(-8.8, 18.44) * mm, "end": v(-18.44, 8.8) * mm});
            skLineSegment(sketch, "E373", {"start": v(-18.44, 8.8) * mm, "end": v(-18.44, -8.8) * mm});
            skLineSegment(sketch, "E374", {"start": v(-18.44, -8.8) * mm, "end": v(-8.8, -18.44) * mm});
            skLineSegment(sketch, "E375", {"start": v(-8.8, -18.44) * mm, "end": v(8.8, -18.44) * mm});
            skLineSegment(sketch, "E376", {"start": v(8.8, -18.44) * mm, "end": v(18.44, -8.8) * mm});
            skLineSegment(sketch, "E377", {"start": v(18.44, -8.8) * mm, "end": v(18.44, 8.8) * mm});
            skLineSegment(sketch, "E378", {"start": v(17.72, 8.5) * mm, "end": v(8.5, 17.72) * mm});
            skLineSegment(sketch, "E379", {"start": v(8.5, 17.72) * mm, "end": v(-8.5, 17.72) * mm});
            skLineSegment(sketch, "E380", {"start": v(-8.5, 17.72) * mm, "end": v(-17.72, 8.5) * mm});
            skLineSegment(sketch, "E381", {"start": v(-17.72, 8.5) * mm, "end": v(-17.72, -8.5) * mm});
            skLineSegment(sketch, "E382", {"start": v(-17.72, -8.5) * mm, "end": v(-8.5, -17.72) * mm});
            skLineSegment(sketch, "E383", {"start": v(-8.5, -17.72) * mm, "end": v(8.5, -17.72) * mm});
            skLineSegment(sketch, "E384", {"start": v(8.5, -17.72) * mm, "end": v(17.72, -8.5) * mm});
            skLineSegment(sketch, "E385", {"start": v(17.72, -8.5) * mm, "end": v(17.72, 8.5) * mm});
            skLineSegment(sketch, "E386", {"start": v(0, -21.83) * mm, "end": v(-21.83, 0) * mm});
            skLineSegment(sketch, "E387", {"start": v(-21.83, 0) * mm, "end": v(0, 21.83) * mm});
            skLineSegment(sketch, "E388", {"start": v(0, 21.83) * mm, "end": v(21.83, 0) * mm});
            skLineSegment(sketch, "E389", {"start": v(21.83, 0) * mm, "end": v(0, -21.83) * mm});
            skLineSegment(sketch, "E390", {"start": v(0, -22.85) * mm, "end": v(-22.85, 0) * mm});
            skLineSegment(sketch, "E391", {"start": v(-22.85, 0) * mm, "end": v(0, 22.85) * mm});
            skLineSegment(sketch, "E392", {"start": v(0, 22.85) * mm, "end": v(22.85, 0) * mm});
            skLineSegment(sketch, "E393", {"start": v(22.85, 0) * mm, "end": v(0, -22.85) * mm});
            skSolve(sketch);
        }
        {
            var Q0;
            {var subQ5=sQuery(id+"F0.wireOp",EDGE,"E365");var subQ6=sQuery(id+"F0.wireOp",EDGE,"E362");var subQ7=makeQuery(id+"F0.imprint","INTERSECT",VERTEX,{"derivedFrom":[subQ6,subQ5]});Q0=makeQuery(id+"F0.imprint","IMPRINT",FACE,{"disambiguationData":[TD([[makeQuery(id+"F0.imprint","IMPRINT",EDGE,{"disambiguationData":[TD([[subQ7,-1.0]])],"derivedFrom":subQ6}),1.0]])]});}
            var Q1;
            {var subQ6=sQuery(id+"F0.wireOp",EDGE,"E363");var subQ8=sQuery(id+"F0.wireOp",EDGE,"E362");var subQ9=makeQuery(id+"F0.imprint","INTERSECT",VERTEX,{"derivedFrom":[subQ8,subQ6]});Q1=makeQuery(id+"F0.imprint","IMPRINT",FACE,{"disambiguationData":[TD([[makeQuery(id+"F0.imprint","IMPRINT",EDGE,{"disambiguationData":[TD([[subQ9,1.0]])],"derivedFrom":subQ8}),1.0]])]});}
            var Q2;
            {var subQ5=sQuery(id+"F0.wireOp",EDGE,"E364");var subQ7=sQuery(id+"F0.wireOp",EDGE,"E363");var subQ8=makeQuery(id+"F0.imprint","INTERSECT",VERTEX,{"derivedFrom":[subQ7,subQ5]});Q2=makeQuery(id+"F0.imprint","IMPRINT",FACE,{"disambiguationData":[TD([[makeQuery(id+"F0.imprint","IMPRINT",EDGE,{"disambiguationData":[TD([[subQ8,1.0]])],"derivedFrom":subQ7}),1.0]])]});}
            var Q3;
            {var subQ6=sQuery(id+"F0.wireOp",EDGE,"E365");var subQ7=sQuery(id+"F0.wireOp",EDGE,"E364");var subQ8=makeQuery(id+"F0.imprint","INTERSECT",VERTEX,{"derivedFrom":[subQ7,subQ6]});Q3=makeQuery(id+"F0.imprint","IMPRINT",FACE,{"disambiguationData":[TD([[makeQuery(id+"F0.imprint","IMPRINT",EDGE,{"disambiguationData":[TD([[subQ8,1.0]])],"derivedFrom":subQ7}),1.0]])]});}
            var Q4;
            {var subQ0=sQuery(id+"F0.wireOp",EDGE,"E376");var subQ3=sQuery(id+"F0.wireOp",EDGE,"E366");var subQ4=makeQuery(id+"F0.imprint","INTERSECT",VERTEX,{"derivedFrom":[subQ3,subQ0]});Q4=makeQuery(id+"F0.imprint","IMPRINT",FACE,{"disambiguationData":[TD([[makeQuery(id+"F0.imprint","IMPRINT",EDGE,{"disambiguationData":[TD([[subQ4,-1.0]])],"derivedFrom":subQ3}),1.0]])]});}
            var Q5;
            {var subQ3=sQuery(id+"F0.wireOp",EDGE,"E366");var subQ5=sQuery(id+"F0.wireOp",EDGE,"E374");var subQ6=makeQuery(id+"F0.imprint","INTERSECT",VERTEX,{"derivedFrom":[subQ3,subQ5]});Q5=makeQuery(id+"F0.imprint","IMPRINT",FACE,{"disambiguationData":[TD([[makeQuery(id+"F0.imprint","IMPRINT",EDGE,{"disambiguationData":[TD([[subQ6,1.0]])],"derivedFrom":subQ3}),1.0]])]});}
            var Q6;
            {var subQ0=sQuery(id+"F0.wireOp",EDGE,"E374");var subQ3=sQuery(id+"F0.wireOp",EDGE,"E367");var subQ4=makeQuery(id+"F0.imprint","INTERSECT",VERTEX,{"derivedFrom":[subQ3,subQ0]});Q6=makeQuery(id+"F0.imprint","IMPRINT",FACE,{"disambiguationData":[TD([[makeQuery(id+"F0.imprint","IMPRINT",EDGE,{"disambiguationData":[TD([[subQ4,-1.0]])],"derivedFrom":subQ3}),1.0]])]});}
            var Q7;
            {var subQ1=sQuery(id+"F0.wireOp",EDGE,"E372");var subQ8=sQuery(id+"F0.wireOp",EDGE,"E367");var subQ10=makeQuery(id+"F0.imprint","INTERSECT",VERTEX,{"derivedFrom":[subQ8,subQ1]});Q7=makeQuery(id+"F0.imprint","IMPRINT",FACE,{"disambiguationData":[TD([[makeQuery(id+"F0.imprint","IMPRINT",EDGE,{"disambiguationData":[TD([[subQ10,1.0]])],"derivedFrom":subQ8}),1.0]])]});}
            var Q8;
            {var subQ0=sQuery(id+"F0.wireOp",EDGE,"E372");var subQ3=sQuery(id+"F0.wireOp",EDGE,"E368");var subQ4=makeQuery(id+"F0.imprint","INTERSECT",VERTEX,{"derivedFrom":[subQ3,subQ0]});Q8=makeQuery(id+"F0.imprint","IMPRINT",FACE,{"disambiguationData":[TD([[makeQuery(id+"F0.imprint","IMPRINT",EDGE,{"disambiguationData":[TD([[subQ4,-1.0]])],"derivedFrom":subQ3}),1.0]])]});}
            var Q9;
            {var subQ1=sQuery(id+"F0.wireOp",EDGE,"E370");var subQ8=sQuery(id+"F0.wireOp",EDGE,"E368");var subQ11=makeQuery(id+"F0.imprint","INTERSECT",VERTEX,{"derivedFrom":[subQ8,subQ1]});Q9=makeQuery(id+"F0.imprint","IMPRINT",FACE,{"disambiguationData":[TD([[makeQuery(id+"F0.imprint","IMPRINT",EDGE,{"disambiguationData":[TD([[subQ11,1.0]])],"derivedFrom":subQ8}),1.0]])]});}
            var Q10;
            {var subQ1=sQuery(id+"F0.wireOp",EDGE,"E370");var subQ9=sQuery(id+"F0.wireOp",EDGE,"E369");var subQ11=makeQuery(id+"F0.imprint","INTERSECT",VERTEX,{"derivedFrom":[subQ9,subQ1]});Q10=makeQuery(id+"F0.imprint","IMPRINT",FACE,{"disambiguationData":[TD([[makeQuery(id+"F0.imprint","IMPRINT",EDGE,{"disambiguationData":[TD([[subQ11,-1.0]])],"derivedFrom":subQ9}),1.0]])]});}
            var Q11;
            {var subQ1=sQuery(id+"F0.wireOp",EDGE,"E376");var subQ8=sQuery(id+"F0.wireOp",EDGE,"E369");var subQ10=makeQuery(id+"F0.imprint","INTERSECT",VERTEX,{"derivedFrom":[subQ8,subQ1]});Q11=makeQuery(id+"F0.imprint","IMPRINT",FACE,{"disambiguationData":[TD([[makeQuery(id+"F0.imprint","IMPRINT",EDGE,{"disambiguationData":[TD([[subQ10,1.0]])],"derivedFrom":subQ8}),1.0]])]});}
            var Q12;
            {var subQ3=sQuery(id+"F0.wireOp",EDGE,"E371");var subQ8=sQuery(id+"F0.wireOp",EDGE,"E392");var subQ9=makeQuery(id+"F0.imprint","INTERSECT",VERTEX,{"derivedFrom":[subQ3,subQ8]});Q12=makeQuery(id+"F0.imprint","IMPRINT",FACE,{"disambiguationData":[TD([[makeQuery(id+"F0.imprint","IMPRINT",EDGE,{"disambiguationData":[TD([[subQ9,-1.0]])],"derivedFrom":subQ3}),-1.0]])]});}
            var Q13;
            {var subQ3=sQuery(id+"F0.wireOp",EDGE,"E373");var subQ8=sQuery(id+"F0.wireOp",EDGE,"E391");var subQ9=makeQuery(id+"F0.imprint","INTERSECT",VERTEX,{"derivedFrom":[subQ3,subQ8]});Q13=makeQuery(id+"F0.imprint","IMPRINT",FACE,{"disambiguationData":[TD([[makeQuery(id+"F0.imprint","IMPRINT",EDGE,{"disambiguationData":[TD([[subQ9,-1.0]])],"derivedFrom":subQ3}),-1.0]])]});}
            var Q14;
            {var subQ3=sQuery(id+"F0.wireOp",EDGE,"E375");var subQ6=sQuery(id+"F0.wireOp",EDGE,"E390");var subQ8=makeQuery(id+"F0.imprint","INTERSECT",VERTEX,{"derivedFrom":[subQ3,subQ6]});Q14=makeQuery(id+"F0.imprint","IMPRINT",FACE,{"disambiguationData":[TD([[makeQuery(id+"F0.imprint","IMPRINT",EDGE,{"disambiguationData":[TD([[subQ8,-1.0]])],"derivedFrom":subQ3}),-1.0]])]});}
            var Q15;
            {var subQ3=sQuery(id+"F0.wireOp",EDGE,"E377");var subQ6=sQuery(id+"F0.wireOp",EDGE,"E393");var subQ7=makeQuery(id+"F0.imprint","INTERSECT",VERTEX,{"derivedFrom":[subQ3,subQ6]});Q15=makeQuery(id+"F0.imprint","IMPRINT",FACE,{"disambiguationData":[TD([[makeQuery(id+"F0.imprint","IMPRINT",EDGE,{"disambiguationData":[TD([[subQ7,-1.0]])],"derivedFrom":subQ3}),-1.0]])]});}
            var Q16;
            {var subQ0=sQuery(id+"F0.wireOp",EDGE,"E376");var subQ1=sQuery(id+"F0.wireOp",EDGE,"E362");var subQ2=makeQuery(id+"F0.imprint","INTERSECT",VERTEX,{"derivedFrom":[subQ1,subQ0]});Q16=makeQuery(id+"F0.imprint","IMPRINT",FACE,{"disambiguationData":[TD([[makeQuery(id+"F0.imprint","IMPRINT",EDGE,{"disambiguationData":[TD([[subQ2,-1.0]])],"derivedFrom":subQ1}),1.0]])]});}
            var Q17;
            {var subQ0=sQuery(id+"F0.wireOp",EDGE,"E382");var subQ1=sQuery(id+"F0.wireOp",EDGE,"E362");var subQ2=makeQuery(id+"F0.imprint","INTERSECT",VERTEX,{"derivedFrom":[subQ1,subQ0]});Q17=makeQuery(id+"F0.imprint","IMPRINT",FACE,{"disambiguationData":[TD([[makeQuery(id+"F0.imprint","IMPRINT",EDGE,{"disambiguationData":[TD([[subQ2,-1.0]])],"derivedFrom":subQ1}),1.0]])]});}
            var Q18;
            {var subQ0=sQuery(id+"F0.wireOp",EDGE,"E374");var subQ1=sQuery(id+"F0.wireOp",EDGE,"E363");var subQ2=makeQuery(id+"F0.imprint","INTERSECT",VERTEX,{"derivedFrom":[subQ1,subQ0]});Q18=makeQuery(id+"F0.imprint","IMPRINT",FACE,{"disambiguationData":[TD([[makeQuery(id+"F0.imprint","IMPRINT",EDGE,{"disambiguationData":[TD([[subQ2,-1.0]])],"derivedFrom":subQ1}),1.0]])]});}
            var Q19;
            {var subQ0=sQuery(id+"F0.wireOp",EDGE,"E380");var subQ1=sQuery(id+"F0.wireOp",EDGE,"E363");var subQ2=makeQuery(id+"F0.imprint","INTERSECT",VERTEX,{"derivedFrom":[subQ1,subQ0]});Q19=makeQuery(id+"F0.imprint","IMPRINT",FACE,{"disambiguationData":[TD([[makeQuery(id+"F0.imprint","IMPRINT",EDGE,{"disambiguationData":[TD([[subQ2,-1.0]])],"derivedFrom":subQ1}),1.0]])]});}
            var Q20;
            {var subQ0=sQuery(id+"F0.wireOp",EDGE,"E372");var subQ1=sQuery(id+"F0.wireOp",EDGE,"E364");var subQ2=makeQuery(id+"F0.imprint","INTERSECT",VERTEX,{"derivedFrom":[subQ1,subQ0]});Q20=makeQuery(id+"F0.imprint","IMPRINT",FACE,{"disambiguationData":[TD([[makeQuery(id+"F0.imprint","IMPRINT",EDGE,{"disambiguationData":[TD([[subQ2,-1.0]])],"derivedFrom":subQ1}),1.0]])]});}
            var Q21;
            {var subQ0=sQuery(id+"F0.wireOp",EDGE,"E378");var subQ1=sQuery(id+"F0.wireOp",EDGE,"E364");var subQ2=makeQuery(id+"F0.imprint","INTERSECT",VERTEX,{"derivedFrom":[subQ1,subQ0]});Q21=makeQuery(id+"F0.imprint","IMPRINT",FACE,{"disambiguationData":[TD([[makeQuery(id+"F0.imprint","IMPRINT",EDGE,{"disambiguationData":[TD([[subQ2,-1.0]])],"derivedFrom":subQ1}),1.0]])]});}
            var Q22;
            {var subQ0=sQuery(id+"F0.wireOp",EDGE,"E370");var subQ1=sQuery(id+"F0.wireOp",EDGE,"E365");var subQ2=makeQuery(id+"F0.imprint","INTERSECT",VERTEX,{"derivedFrom":[subQ1,subQ0]});Q22=makeQuery(id+"F0.imprint","IMPRINT",FACE,{"disambiguationData":[TD([[makeQuery(id+"F0.imprint","IMPRINT",EDGE,{"disambiguationData":[TD([[subQ2,-1.0]])],"derivedFrom":subQ1}),1.0]])]});}
            var Q23;
            {var subQ0=sQuery(id+"F0.wireOp",EDGE,"E384");var subQ1=sQuery(id+"F0.wireOp",EDGE,"E365");var subQ2=makeQuery(id+"F0.imprint","INTERSECT",VERTEX,{"derivedFrom":[subQ1,subQ0]});Q23=makeQuery(id+"F0.imprint","IMPRINT",FACE,{"disambiguationData":[TD([[makeQuery(id+"F0.imprint","IMPRINT",EDGE,{"disambiguationData":[TD([[subQ2,-1.0]])],"derivedFrom":subQ1}),1.0]])]});}
            var Q24;
            {var subQ0=sQuery(id+"F0.wireOp",EDGE,"E392");var subQ1=sQuery(id+"F0.wireOp",EDGE,"E371");var subQ2=makeQuery(id+"F0.imprint","INTERSECT",VERTEX,{"derivedFrom":[subQ1,subQ0]});Q24=makeQuery(id+"F0.imprint","IMPRINT",FACE,{"disambiguationData":[TD([[makeQuery(id+"F0.imprint","IMPRINT",EDGE,{"disambiguationData":[TD([[subQ2,-1.0]])],"derivedFrom":subQ1}),1.0]])]});}
            var Q25;
            {var subQ0=sQuery(id+"F0.wireOp",EDGE,"E391");var subQ1=sQuery(id+"F0.wireOp",EDGE,"E371");var subQ2=makeQuery(id+"F0.imprint","INTERSECT",VERTEX,{"derivedFrom":[subQ1,subQ0]});Q25=makeQuery(id+"F0.imprint","IMPRINT",FACE,{"disambiguationData":[TD([[makeQuery(id+"F0.imprint","IMPRINT",EDGE,{"disambiguationData":[TD([[subQ2,1.0]])],"derivedFrom":subQ1}),1.0]])]});}
            var Q26;
            {var subQ0=sQuery(id+"F0.wireOp",EDGE,"E391");var subQ1=sQuery(id+"F0.wireOp",EDGE,"E373");var subQ2=makeQuery(id+"F0.imprint","INTERSECT",VERTEX,{"derivedFrom":[subQ1,subQ0]});Q26=makeQuery(id+"F0.imprint","IMPRINT",FACE,{"disambiguationData":[TD([[makeQuery(id+"F0.imprint","IMPRINT",EDGE,{"disambiguationData":[TD([[subQ2,-1.0]])],"derivedFrom":subQ1}),1.0]])]});}
            var Q27;
            {var subQ0=sQuery(id+"F0.wireOp",EDGE,"E390");var subQ1=sQuery(id+"F0.wireOp",EDGE,"E373");var subQ2=makeQuery(id+"F0.imprint","INTERSECT",VERTEX,{"derivedFrom":[subQ1,subQ0]});Q27=makeQuery(id+"F0.imprint","IMPRINT",FACE,{"disambiguationData":[TD([[makeQuery(id+"F0.imprint","IMPRINT",EDGE,{"disambiguationData":[TD([[subQ2,1.0]])],"derivedFrom":subQ1}),1.0]])]});}
            var Q28;
            {var subQ0=sQuery(id+"F0.wireOp",EDGE,"E390");var subQ1=sQuery(id+"F0.wireOp",EDGE,"E375");var subQ2=makeQuery(id+"F0.imprint","INTERSECT",VERTEX,{"derivedFrom":[subQ1,subQ0]});Q28=makeQuery(id+"F0.imprint","IMPRINT",FACE,{"disambiguationData":[TD([[makeQuery(id+"F0.imprint","IMPRINT",EDGE,{"disambiguationData":[TD([[subQ2,-1.0]])],"derivedFrom":subQ1}),1.0]])]});}
            var Q29;
            {var subQ0=sQuery(id+"F0.wireOp",EDGE,"E393");var subQ1=sQuery(id+"F0.wireOp",EDGE,"E375");var subQ2=makeQuery(id+"F0.imprint","INTERSECT",VERTEX,{"derivedFrom":[subQ1,subQ0]});Q29=makeQuery(id+"F0.imprint","IMPRINT",FACE,{"disambiguationData":[TD([[makeQuery(id+"F0.imprint","IMPRINT",EDGE,{"disambiguationData":[TD([[subQ2,1.0]])],"derivedFrom":subQ1}),1.0]])]});}
            var Q30;
            {var subQ0=sQuery(id+"F0.wireOp",EDGE,"E393");var subQ1=sQuery(id+"F0.wireOp",EDGE,"E377");var subQ2=makeQuery(id+"F0.imprint","INTERSECT",VERTEX,{"derivedFrom":[subQ1,subQ0]});Q30=makeQuery(id+"F0.imprint","IMPRINT",FACE,{"disambiguationData":[TD([[makeQuery(id+"F0.imprint","IMPRINT",EDGE,{"disambiguationData":[TD([[subQ2,-1.0]])],"derivedFrom":subQ1}),1.0]])]});}
            var Q31;
            {var subQ0=sQuery(id+"F0.wireOp",EDGE,"E392");var subQ1=sQuery(id+"F0.wireOp",EDGE,"E377");var subQ2=makeQuery(id+"F0.imprint","INTERSECT",VERTEX,{"derivedFrom":[subQ1,subQ0]});Q31=makeQuery(id+"F0.imprint","IMPRINT",FACE,{"disambiguationData":[TD([[makeQuery(id+"F0.imprint","IMPRINT",EDGE,{"disambiguationData":[TD([[subQ2,1.0]])],"derivedFrom":subQ1}),1.0]])]});}
            var Q32;
            {var subQ0=sQuery(id+"F0.wireOp",EDGE,"E382");var subQ1=sQuery(id+"F0.wireOp",EDGE,"E363");var subQ2=makeQuery(id+"F0.imprint","INTERSECT",VERTEX,{"derivedFrom":[subQ1,subQ0]});Q32=makeQuery(id+"F0.imprint","IMPRINT",FACE,{"disambiguationData":[TD([[makeQuery(id+"F0.imprint","IMPRINT",EDGE,{"disambiguationData":[TD([[subQ2,-1.0]])],"derivedFrom":subQ1}),1.0]])]});}
            var Q33;
            {var subQ0=sQuery(id+"F0.wireOp",EDGE,"E389");var subQ1=sQuery(id+"F0.wireOp",EDGE,"E377");var subQ2=makeQuery(id+"F0.imprint","INTERSECT",VERTEX,{"derivedFrom":[subQ1,subQ0]});Q33=makeQuery(id+"F0.imprint","IMPRINT",FACE,{"disambiguationData":[TD([[makeQuery(id+"F0.imprint","IMPRINT",EDGE,{"disambiguationData":[TD([[subQ2,-1.0]])],"derivedFrom":subQ1}),1.0]])]});}
            var Q34;
            {var subQ0=sQuery(id+"F0.wireOp",EDGE,"E378");var subQ1=sQuery(id+"F0.wireOp",EDGE,"E364");var subQ2=makeQuery(id+"F0.imprint","INTERSECT",VERTEX,{"derivedFrom":[subQ1,subQ0]});Q34=makeQuery(id+"F0.imprint","IMPRINT",FACE,{"disambiguationData":[TD([[makeQuery(id+"F0.imprint","IMPRINT",EDGE,{"disambiguationData":[TD([[subQ2,-1.0]])],"derivedFrom":subQ1}),-1.0]])]});}
            var Q35;
            {var subQ0=sQuery(id+"F0.wireOp",EDGE,"E392");var subQ1=sQuery(id+"F0.wireOp",EDGE,"E369");var subQ2=makeQuery(id+"F0.imprint","INTERSECT",VERTEX,{"derivedFrom":[subQ1,subQ0]});Q35=makeQuery(id+"F0.imprint","IMPRINT",FACE,{"disambiguationData":[TD([[makeQuery(id+"F0.imprint","IMPRINT",EDGE,{"disambiguationData":[TD([[subQ2,-1.0]])],"derivedFrom":subQ1}),1.0]])]});}
            var Q36;
            {var subQ0=sQuery(id+"F0.wireOp",EDGE,"E382");var subQ1=sQuery(id+"F0.wireOp",EDGE,"E362");var subQ2=makeQuery(id+"F0.imprint","INTERSECT",VERTEX,{"derivedFrom":[subQ1,subQ0]});Q36=makeQuery(id+"F0.imprint","IMPRINT",FACE,{"disambiguationData":[TD([[makeQuery(id+"F0.imprint","IMPRINT",EDGE,{"disambiguationData":[TD([[subQ2,-1.0]])],"derivedFrom":subQ1}),-1.0]])]});}
            var Q37;
            {var subQ0=sQuery(id+"F0.wireOp",EDGE,"E391");var subQ1=sQuery(id+"F0.wireOp",EDGE,"E368");var subQ2=makeQuery(id+"F0.imprint","INTERSECT",VERTEX,{"derivedFrom":[subQ1,subQ0]});Q37=makeQuery(id+"F0.imprint","IMPRINT",FACE,{"disambiguationData":[TD([[makeQuery(id+"F0.imprint","IMPRINT",EDGE,{"disambiguationData":[TD([[subQ2,-1.0]])],"derivedFrom":subQ1}),1.0]])]});}
            var Q38;
            {var subQ0=sQuery(id+"F0.wireOp",EDGE,"E376");var subQ1=sQuery(id+"F0.wireOp",EDGE,"E362");var subQ2=makeQuery(id+"F0.imprint","INTERSECT",VERTEX,{"derivedFrom":[subQ1,subQ0]});Q38=makeQuery(id+"F0.imprint","IMPRINT",FACE,{"disambiguationData":[TD([[makeQuery(id+"F0.imprint","IMPRINT",EDGE,{"disambiguationData":[TD([[subQ2,-1.0]])],"derivedFrom":subQ1}),-1.0]])]});}
            var Q39;
            {var subQ0=sQuery(id+"F0.wireOp",EDGE,"E387");var subQ1=sQuery(id+"F0.wireOp",EDGE,"E373");var subQ2=makeQuery(id+"F0.imprint","INTERSECT",VERTEX,{"derivedFrom":[subQ1,subQ0]});Q39=makeQuery(id+"F0.imprint","IMPRINT",FACE,{"disambiguationData":[TD([[makeQuery(id+"F0.imprint","IMPRINT",EDGE,{"disambiguationData":[TD([[subQ2,-1.0]])],"derivedFrom":subQ1}),1.0]])]});}
            var Q40;
            {var subQ0=sQuery(id+"F0.wireOp",EDGE,"E388");var subQ1=sQuery(id+"F0.wireOp",EDGE,"E371");var subQ2=makeQuery(id+"F0.imprint","INTERSECT",VERTEX,{"derivedFrom":[subQ1,subQ0]});Q40=makeQuery(id+"F0.imprint","IMPRINT",FACE,{"disambiguationData":[TD([[makeQuery(id+"F0.imprint","IMPRINT",EDGE,{"disambiguationData":[TD([[subQ2,-1.0]])],"derivedFrom":subQ1}),1.0]])]});}
            var Q41;
            {var subQ0=sQuery(id+"F0.wireOp",EDGE,"E390");var subQ1=sQuery(id+"F0.wireOp",EDGE,"E367");var subQ2=makeQuery(id+"F0.imprint","INTERSECT",VERTEX,{"derivedFrom":[subQ1,subQ0]});Q41=makeQuery(id+"F0.imprint","IMPRINT",FACE,{"disambiguationData":[TD([[makeQuery(id+"F0.imprint","IMPRINT",EDGE,{"disambiguationData":[TD([[subQ2,-1.0]])],"derivedFrom":subQ1}),1.0]])]});}
            var Q42;
            {var subQ0=sQuery(id+"F0.wireOp",EDGE,"E386");var subQ1=sQuery(id+"F0.wireOp",EDGE,"E375");var subQ2=makeQuery(id+"F0.imprint","INTERSECT",VERTEX,{"derivedFrom":[subQ1,subQ0]});Q42=makeQuery(id+"F0.imprint","IMPRINT",FACE,{"disambiguationData":[TD([[makeQuery(id+"F0.imprint","IMPRINT",EDGE,{"disambiguationData":[TD([[subQ2,-1.0]])],"derivedFrom":subQ1}),1.0]])]});}
            var Q43;
            {var subQ0=sQuery(id+"F0.wireOp",EDGE,"E391");var subQ1=sQuery(id+"F0.wireOp",EDGE,"E363");var subQ2=makeQuery(id+"F0.imprint","INTERSECT",VERTEX,{"derivedFrom":[subQ1,subQ0]});Q43=makeQuery(id+"F0.imprint","IMPRINT",FACE,{"disambiguationData":[TD([[makeQuery(id+"F0.imprint","IMPRINT",EDGE,{"disambiguationData":[TD([[subQ2,-1.0]])],"derivedFrom":subQ1}),1.0]])]});}
            var Q44;
            {var subQ0=sQuery(id+"F0.wireOp",EDGE,"E380");var subQ1=sQuery(id+"F0.wireOp",EDGE,"E363");var subQ2=makeQuery(id+"F0.imprint","INTERSECT",VERTEX,{"derivedFrom":[subQ1,subQ0]});Q44=makeQuery(id+"F0.imprint","IMPRINT",FACE,{"disambiguationData":[TD([[makeQuery(id+"F0.imprint","IMPRINT",EDGE,{"disambiguationData":[TD([[subQ2,-1.0]])],"derivedFrom":subQ1}),-1.0]])]});}
            var Q45;
            {var subQ0=sQuery(id+"F0.wireOp",EDGE,"E392");var subQ1=sQuery(id+"F0.wireOp",EDGE,"E364");var subQ2=makeQuery(id+"F0.imprint","INTERSECT",VERTEX,{"derivedFrom":[subQ1,subQ0]});Q45=makeQuery(id+"F0.imprint","IMPRINT",FACE,{"disambiguationData":[TD([[makeQuery(id+"F0.imprint","IMPRINT",EDGE,{"disambiguationData":[TD([[subQ2,-1.0]])],"derivedFrom":subQ1}),1.0]])]});}
            var Q46;
            {var subQ0=sQuery(id+"F0.wireOp",EDGE,"E380");var subQ1=sQuery(id+"F0.wireOp",EDGE,"E364");var subQ2=makeQuery(id+"F0.imprint","INTERSECT",VERTEX,{"derivedFrom":[subQ1,subQ0]});Q46=makeQuery(id+"F0.imprint","IMPRINT",FACE,{"disambiguationData":[TD([[makeQuery(id+"F0.imprint","IMPRINT",EDGE,{"disambiguationData":[TD([[subQ2,-1.0]])],"derivedFrom":subQ1}),1.0]])]});}
            var Q47;
            {var subQ0=sQuery(id+"F0.wireOp",EDGE,"E384");var subQ1=sQuery(id+"F0.wireOp",EDGE,"E362");var subQ2=makeQuery(id+"F0.imprint","INTERSECT",VERTEX,{"derivedFrom":[subQ1,subQ0]});Q47=makeQuery(id+"F0.imprint","IMPRINT",FACE,{"disambiguationData":[TD([[makeQuery(id+"F0.imprint","IMPRINT",EDGE,{"disambiguationData":[TD([[subQ2,-1.0]])],"derivedFrom":subQ1}),1.0]])]});}
            var Q48;
            {var subQ0=sQuery(id+"F0.wireOp",EDGE,"E386");var subQ1=sQuery(id+"F0.wireOp",EDGE,"E366");var subQ2=makeQuery(id+"F0.imprint","INTERSECT",VERTEX,{"derivedFrom":[subQ1,subQ0]});Q48=makeQuery(id+"F0.imprint","IMPRINT",FACE,{"disambiguationData":[TD([[makeQuery(id+"F0.imprint","IMPRINT",EDGE,{"disambiguationData":[TD([[subQ2,-1.0]])],"derivedFrom":subQ1}),1.0]])]});}
            var Q49;
            {var subQ0=sQuery(id+"F0.wireOp",EDGE,"E393");var subQ1=sQuery(id+"F0.wireOp",EDGE,"E365");var subQ2=makeQuery(id+"F0.imprint","INTERSECT",VERTEX,{"derivedFrom":[subQ1,subQ0]});Q49=makeQuery(id+"F0.imprint","IMPRINT",FACE,{"disambiguationData":[TD([[makeQuery(id+"F0.imprint","IMPRINT",EDGE,{"disambiguationData":[TD([[subQ2,-1.0]])],"derivedFrom":subQ1}),1.0]])]});}
            var Q50;
            {var subQ0=sQuery(id+"F0.wireOp",EDGE,"E378");var subQ1=sQuery(id+"F0.wireOp",EDGE,"E365");var subQ2=makeQuery(id+"F0.imprint","INTERSECT",VERTEX,{"derivedFrom":[subQ1,subQ0]});Q50=makeQuery(id+"F0.imprint","IMPRINT",FACE,{"disambiguationData":[TD([[makeQuery(id+"F0.imprint","IMPRINT",EDGE,{"disambiguationData":[TD([[subQ2,-1.0]])],"derivedFrom":subQ1}),1.0]])]});}
            var Q51;
            {var subQ0=sQuery(id+"F0.wireOp",EDGE,"E390");var subQ1=sQuery(id+"F0.wireOp",EDGE,"E362");var subQ2=makeQuery(id+"F0.imprint","INTERSECT",VERTEX,{"derivedFrom":[subQ1,subQ0]});Q51=makeQuery(id+"F0.imprint","IMPRINT",FACE,{"disambiguationData":[TD([[makeQuery(id+"F0.imprint","IMPRINT",EDGE,{"disambiguationData":[TD([[subQ2,-1.0]])],"derivedFrom":subQ1}),1.0]])]});}
            var Q52;
            {var subQ0=sQuery(id+"F0.wireOp",EDGE,"E388");var subQ1=sQuery(id+"F0.wireOp",EDGE,"E368");var subQ2=makeQuery(id+"F0.imprint","INTERSECT",VERTEX,{"derivedFrom":[subQ1,subQ0]});Q52=makeQuery(id+"F0.imprint","IMPRINT",FACE,{"disambiguationData":[TD([[makeQuery(id+"F0.imprint","IMPRINT",EDGE,{"disambiguationData":[TD([[subQ2,-1.0]])],"derivedFrom":subQ1}),1.0]])]});}
            var Q53;
            {var subQ0=sQuery(id+"F0.wireOp",EDGE,"E389");var subQ1=sQuery(id+"F0.wireOp",EDGE,"E369");var subQ2=makeQuery(id+"F0.imprint","INTERSECT",VERTEX,{"derivedFrom":[subQ1,subQ0]});Q53=makeQuery(id+"F0.imprint","IMPRINT",FACE,{"disambiguationData":[TD([[makeQuery(id+"F0.imprint","IMPRINT",EDGE,{"disambiguationData":[TD([[subQ2,-1.0]])],"derivedFrom":subQ1}),1.0]])]});}
            var Q54;
            {var subQ0=sQuery(id+"F0.wireOp",EDGE,"E392");var subQ1=sQuery(id+"F0.wireOp",EDGE,"E365");var subQ2=makeQuery(id+"F0.imprint","INTERSECT",VERTEX,{"derivedFrom":[subQ1,subQ0]});Q54=makeQuery(id+"F0.imprint","IMPRINT",FACE,{"disambiguationData":[TD([[makeQuery(id+"F0.imprint","IMPRINT",EDGE,{"disambiguationData":[TD([[subQ2,-1.0]])],"derivedFrom":subQ1}),1.0]])]});}
            var Q55;
            {var subQ0=sQuery(id+"F0.wireOp",EDGE,"E387");var subQ1=sQuery(id+"F0.wireOp",EDGE,"E367");var subQ2=makeQuery(id+"F0.imprint","INTERSECT",VERTEX,{"derivedFrom":[subQ1,subQ0]});Q55=makeQuery(id+"F0.imprint","IMPRINT",FACE,{"disambiguationData":[TD([[makeQuery(id+"F0.imprint","IMPRINT",EDGE,{"disambiguationData":[TD([[subQ2,-1.0]])],"derivedFrom":subQ1}),1.0]])]});}
            var Q56;
            {var subQ0=sQuery(id+"F0.wireOp",EDGE,"E386");var subQ1=sQuery(id+"F0.wireOp",EDGE,"E362");var subQ2=makeQuery(id+"F0.imprint","INTERSECT",VERTEX,{"derivedFrom":[subQ1,subQ0]});Q56=makeQuery(id+"F0.imprint","IMPRINT",FACE,{"disambiguationData":[TD([[makeQuery(id+"F0.imprint","IMPRINT",EDGE,{"disambiguationData":[TD([[subQ2,-1.0]])],"derivedFrom":subQ1}),1.0]])]});}
            var Q57;
            {var subQ0=sQuery(id+"F0.wireOp",EDGE,"E393");var subQ1=sQuery(id+"F0.wireOp",EDGE,"E366");var subQ2=makeQuery(id+"F0.imprint","INTERSECT",VERTEX,{"derivedFrom":[subQ1,subQ0]});Q57=makeQuery(id+"F0.imprint","IMPRINT",FACE,{"disambiguationData":[TD([[makeQuery(id+"F0.imprint","IMPRINT",EDGE,{"disambiguationData":[TD([[subQ2,-1.0]])],"derivedFrom":subQ1}),1.0]])]});}
            var Q58;
            {var subQ0=sQuery(id+"F0.wireOp",EDGE,"E391");var subQ1=sQuery(id+"F0.wireOp",EDGE,"E364");var subQ2=makeQuery(id+"F0.imprint","INTERSECT",VERTEX,{"derivedFrom":[subQ1,subQ0]});Q58=makeQuery(id+"F0.imprint","IMPRINT",FACE,{"disambiguationData":[TD([[makeQuery(id+"F0.imprint","IMPRINT",EDGE,{"disambiguationData":[TD([[subQ2,-1.0]])],"derivedFrom":subQ1}),1.0]])]});}
            var Q59;
            {var subQ0=sQuery(id+"F0.wireOp",EDGE,"E388");var subQ1=sQuery(id+"F0.wireOp",EDGE,"E364");var subQ2=makeQuery(id+"F0.imprint","INTERSECT",VERTEX,{"derivedFrom":[subQ1,subQ0]});Q59=makeQuery(id+"F0.imprint","IMPRINT",FACE,{"disambiguationData":[TD([[makeQuery(id+"F0.imprint","IMPRINT",EDGE,{"disambiguationData":[TD([[subQ2,-1.0]])],"derivedFrom":subQ1}),1.0]])]});}
            var Q60;
            {var subQ10=sQuery(id+"F0.wireOp",EDGE,"E228");Q60=makeQuery(id+"F0.imprint","IMPRINT",FACE,{"disambiguationData":[TD([[makeQuery(id+"F0.imprint","IMPRINT",EDGE,{"derivedFrom":subQ10}),1.0]])]});}
            var Q61;
            {var subQ13=sQuery(id+"F0.wireOp",EDGE,"E196");Q61=makeQuery(id+"F0.imprint","IMPRINT",FACE,{"disambiguationData":[TD([[makeQuery(id+"F0.imprint","IMPRINT",EDGE,{"derivedFrom":subQ13}),1.0]])]});}
            var Q62;
            {var subQ6=sQuery(id+"F0.wireOp",EDGE,"E273");Q62=makeQuery(id+"F0.imprint","IMPRINT",FACE,{"disambiguationData":[TD([[makeQuery(id+"F0.imprint","IMPRINT",EDGE,{"derivedFrom":subQ6}),1.0]])]});}
            var Q63;
            {var subQ8=sQuery(id+"F0.wireOp",EDGE,"E182");Q63=makeQuery(id+"F0.imprint","IMPRINT",FACE,{"disambiguationData":[TD([[makeQuery(id+"F0.imprint","IMPRINT",EDGE,{"derivedFrom":subQ8}),1.0]])]});}
            var Q64;
            {var subQ6=sQuery(id+"F0.wireOp",EDGE,"E318");Q64=makeQuery(id+"F0.imprint","IMPRINT",FACE,{"disambiguationData":[TD([[makeQuery(id+"F0.imprint","IMPRINT",EDGE,{"derivedFrom":subQ6}),1.0]])]});}
            var Q65;
            {var subQ12=sQuery(id+"F0.wireOp",EDGE,"E241");Q65=makeQuery(id+"F0.imprint","IMPRINT",FACE,{"disambiguationData":[TD([[makeQuery(id+"F0.imprint","IMPRINT",EDGE,{"derivedFrom":subQ12}),1.0]])]});}
            var Q66;
            {var subQ0=sQuery(id+"F0.wireOp",EDGE,"E389");var subQ1=sQuery(id+"F0.wireOp",EDGE,"E365");var subQ2=makeQuery(id+"F0.imprint","INTERSECT",VERTEX,{"derivedFrom":[subQ1,subQ0]});Q66=makeQuery(id+"F0.imprint","IMPRINT",FACE,{"disambiguationData":[TD([[makeQuery(id+"F0.imprint","IMPRINT",EDGE,{"disambiguationData":[TD([[subQ2,-1.0]])],"derivedFrom":subQ1}),1.0]])]});}
            var Q67;
            {var subQ10=sQuery(id+"F0.wireOp",EDGE,"E331");Q67=makeQuery(id+"F0.imprint","IMPRINT",FACE,{"disambiguationData":[TD([[makeQuery(id+"F0.imprint","IMPRINT",EDGE,{"derivedFrom":subQ10}),1.0]])]});}
            var Q68;
            {var subQ10=sQuery(id+"F0.wireOp",EDGE,"E286");Q68=makeQuery(id+"F0.imprint","IMPRINT",FACE,{"disambiguationData":[TD([[makeQuery(id+"F0.imprint","IMPRINT",EDGE,{"derivedFrom":subQ10}),1.0]])]});}
            var Q69;
            {var subQ0=sQuery(id+"F0.wireOp",EDGE,"E390");var subQ1=sQuery(id+"F0.wireOp",EDGE,"E363");var subQ2=makeQuery(id+"F0.imprint","INTERSECT",VERTEX,{"derivedFrom":[subQ1,subQ0]});Q69=makeQuery(id+"F0.imprint","IMPRINT",FACE,{"disambiguationData":[TD([[makeQuery(id+"F0.imprint","IMPRINT",EDGE,{"disambiguationData":[TD([[subQ2,-1.0]])],"derivedFrom":subQ1}),1.0]])]});}
            var Q70;
            {var subQ0=sQuery(id+"F0.wireOp",EDGE,"E361");var subQ1=sQuery(id+"F0.wireOp",EDGE,"E181");var subQ2=makeQuery(id+"F0.imprint","INTERSECT",VERTEX,{"derivedFrom":[subQ1,subQ0]});Q70=makeQuery(id+"F0.imprint","IMPRINT",FACE,{"disambiguationData":[TD([[makeQuery(id+"F0.imprint","IMPRINT",EDGE,{"disambiguationData":[TD([[subQ2,-1.0]])],"derivedFrom":subQ1}),-1.0]])]});}
            var Q71;
            {var subQ5=sQuery(id+"F0.wireOp",EDGE,"E286");Q71=makeQuery(id+"F0.imprint","IMPRINT",FACE,{"disambiguationData":[TD([[makeQuery(id+"F0.imprint","IMPRINT",EDGE,{"derivedFrom":subQ5}),-1.0]])]});}
            var Q72;
            {var subQ8=sQuery(id+"F0.wireOp",EDGE,"E309");Q72=makeQuery(id+"F0.imprint","IMPRINT",FACE,{"disambiguationData":[TD([[makeQuery(id+"F0.imprint","IMPRINT",EDGE,{"derivedFrom":subQ8}),1.0]])]});}
            var Q73;
            {var subQ0=sQuery(id+"F0.wireOp",EDGE,"E387");var subQ1=sQuery(id+"F0.wireOp",EDGE,"E363");var subQ2=makeQuery(id+"F0.imprint","INTERSECT",VERTEX,{"derivedFrom":[subQ1,subQ0]});Q73=makeQuery(id+"F0.imprint","IMPRINT",FACE,{"disambiguationData":[TD([[makeQuery(id+"F0.imprint","IMPRINT",EDGE,{"disambiguationData":[TD([[subQ2,-1.0]])],"derivedFrom":subQ1}),1.0]])]});}
            var Q74;
            {var subQ9=sQuery(id+"F0.wireOp",EDGE,"E354");Q74=makeQuery(id+"F0.imprint","IMPRINT",FACE,{"disambiguationData":[TD([[makeQuery(id+"F0.imprint","IMPRINT",EDGE,{"derivedFrom":subQ9}),1.0]])]});}
            var Q75;
            {var subQ9=sQuery(id+"F0.wireOp",EDGE,"E137");Q75=makeQuery(id+"F0.imprint","IMPRINT",FACE,{"disambiguationData":[TD([[makeQuery(id+"F0.imprint","IMPRINT",EDGE,{"derivedFrom":subQ9}),1.0]])]});}
            var Q76;
            {var subQ0=sQuery(id+"F0.wireOp",EDGE,"E90");Q76=makeQuery(id+"F0.imprint","IMPRINT",FACE,{"disambiguationData":[TD([[makeQuery(id+"F0.imprint","IMPRINT",EDGE,{"derivedFrom":subQ0}),-1.0]])]});}
            var Q77;
            {var subQ18=sQuery(id+"F0.wireOp",EDGE,"E1");Q77=makeQuery(id+"F0.imprint","IMPRINT",FACE,{"disambiguationData":[TD([[makeQuery(id+"F0.imprint","IMPRINT",EDGE,{"derivedFrom":subQ18}),1.0]])]});}
            var Q78;
            {var subQ0=sQuery(id+"F0.wireOp",EDGE,"E196");Q78=makeQuery(id+"F0.imprint","IMPRINT",FACE,{"disambiguationData":[TD([[makeQuery(id+"F0.imprint","IMPRINT",EDGE,{"derivedFrom":subQ0}),-1.0]])]});}
            var Q79;
            {var subQ17=sQuery(id+"F0.wireOp",EDGE,"E45");Q79=makeQuery(id+"F0.imprint","IMPRINT",FACE,{"disambiguationData":[TD([[makeQuery(id+"F0.imprint","IMPRINT",EDGE,{"derivedFrom":subQ17}),1.0]])]});}
            var Q80;
            {var subQ18=sQuery(id+"F0.wireOp",EDGE,"E92");Q80=makeQuery(id+"F0.imprint","IMPRINT",FACE,{"disambiguationData":[TD([[makeQuery(id+"F0.imprint","IMPRINT",EDGE,{"derivedFrom":subQ18}),1.0]])]});}
            var Q81;
            {var subQ16=sQuery(id+"F0.wireOp",EDGE,"E135");Q81=makeQuery(id+"F0.imprint","IMPRINT",FACE,{"disambiguationData":[TD([[makeQuery(id+"F0.imprint","IMPRINT",EDGE,{"derivedFrom":subQ16}),1.0]])]});}
            var Q82;
            {var subQ17=sQuery(id+"F0.wireOp",EDGE,"E182");Q82=makeQuery(id+"F0.imprint","IMPRINT",FACE,{"disambiguationData":[TD([[makeQuery(id+"F0.imprint","IMPRINT",EDGE,{"derivedFrom":subQ17}),-1.0]])]});}
            var Q83;
            {var subQ0=sQuery(id+"F0.wireOp",EDGE,"E241");Q83=makeQuery(id+"F0.imprint","IMPRINT",FACE,{"disambiguationData":[TD([[makeQuery(id+"F0.imprint","IMPRINT",EDGE,{"derivedFrom":subQ0}),-1.0]])]});}
            var Q84;
            {var subQ9=sQuery(id+"F0.wireOp",EDGE,"E263");Q84=makeQuery(id+"F0.imprint","IMPRINT",FACE,{"disambiguationData":[TD([[makeQuery(id+"F0.imprint","IMPRINT",EDGE,{"derivedFrom":subQ9}),1.0]])]});}
            var Q85;
            {var subQ17=sQuery(id+"F0.wireOp",EDGE,"E47");Q85=makeQuery(id+"F0.imprint","IMPRINT",FACE,{"disambiguationData":[TD([[makeQuery(id+"F0.imprint","IMPRINT",EDGE,{"derivedFrom":subQ17}),1.0]])]});}
            var Q86;
            {var subQ9=sQuery(id+"F0.wireOp",EDGE,"E218");Q86=makeQuery(id+"F0.imprint","IMPRINT",FACE,{"disambiguationData":[TD([[makeQuery(id+"F0.imprint","IMPRINT",EDGE,{"derivedFrom":subQ9}),1.0]])]});}
            var Q87;
            {var subQ16=sQuery(id+"F0.wireOp",EDGE,"E90");Q87=makeQuery(id+"F0.imprint","IMPRINT",FACE,{"disambiguationData":[TD([[makeQuery(id+"F0.imprint","IMPRINT",EDGE,{"derivedFrom":subQ16}),1.0]])]});}
            var Q88;
            {var subQ0=sQuery(id+"F0.wireOp",EDGE,"E393");var subQ1=sQuery(id+"F0.wireOp",EDGE,"E362");var subQ2=makeQuery(id+"F0.imprint","INTERSECT",VERTEX,{"derivedFrom":[subQ1,subQ0]});Q88=makeQuery(id+"F0.imprint","IMPRINT",FACE,{"disambiguationData":[TD([[makeQuery(id+"F0.imprint","IMPRINT",EDGE,{"disambiguationData":[TD([[subQ2,-1.0]])],"derivedFrom":subQ1}),1.0]])]});}
            var Q89;
            {var subQ0=sQuery(id+"F0.wireOp",EDGE,"E135");Q89=makeQuery(id+"F0.imprint","IMPRINT",FACE,{"disambiguationData":[TD([[makeQuery(id+"F0.imprint","IMPRINT",EDGE,{"derivedFrom":subQ0}),-1.0]])]});}
            var Q90;
            {var subQ0=sQuery(id+"F0.wireOp",EDGE,"E331");Q90=makeQuery(id+"F0.imprint","IMPRINT",FACE,{"disambiguationData":[TD([[makeQuery(id+"F0.imprint","IMPRINT",EDGE,{"derivedFrom":subQ0}),-1.0]])]});}
            var Q91;
            {var subQ0=sQuery(id+"F0.wireOp",EDGE,"E271");Q91=makeQuery(id+"F0.imprint","IMPRINT",FACE,{"disambiguationData":[TD([[makeQuery(id+"F0.imprint","IMPRINT",EDGE,{"derivedFrom":subQ0}),-1.0]])]});}
            var Q92;
            {var subQ0=sQuery(id+"F0.wireOp",EDGE,"E316");Q92=makeQuery(id+"F0.imprint","IMPRINT",FACE,{"disambiguationData":[TD([[makeQuery(id+"F0.imprint","IMPRINT",EDGE,{"derivedFrom":subQ0}),-1.0]])]});}
            var Q93;
            {var subQ0=sQuery(id+"F0.wireOp",EDGE,"E226");Q93=makeQuery(id+"F0.imprint","IMPRINT",FACE,{"disambiguationData":[TD([[makeQuery(id+"F0.imprint","IMPRINT",EDGE,{"derivedFrom":subQ0}),-1.0]])]});}
            var Q94;
            {var subQ0=sQuery(id+"F0.wireOp",EDGE,"E45");Q94=makeQuery(id+"F0.imprint","IMPRINT",FACE,{"disambiguationData":[TD([[makeQuery(id+"F0.imprint","IMPRINT",EDGE,{"derivedFrom":subQ0}),-1.0]])]});}
            extrude(context, id + "F1", {"entities" : qUnion([Q0, Q1, Q2, Q3, Q4, Q5, Q6, Q7, Q8, Q9, Q10, Q11, Q12, Q13, Q14, Q15, Q16, Q17, Q18, Q19, Q20, Q21, Q22, Q23, Q24, Q25, Q26, Q27, Q28, Q29, Q30, Q31, Q32, Q33, Q34, Q35, Q36, Q37, Q38, Q39, Q40, Q41, Q42, Q43, Q44, Q45, Q46, Q47, Q48, Q49, Q50, Q51, Q52, Q53, Q54, Q55, Q56, Q57, Q58, Q59, Q60, Q61, Q62, Q63, Q64, Q65, Q66, Q67, Q68, Q69, Q70, Q71, Q72, Q73, Q74, Q75, Q76, Q77, Q78, Q79, Q80, Q81, Q82, Q83, Q84, Q85, Q86, Q87, Q88, Q89, Q90, Q91, Q92, Q93, Q94]), "depth" : 3 * mm, "offsetDistance" : 25 * mm});
        }
    });
